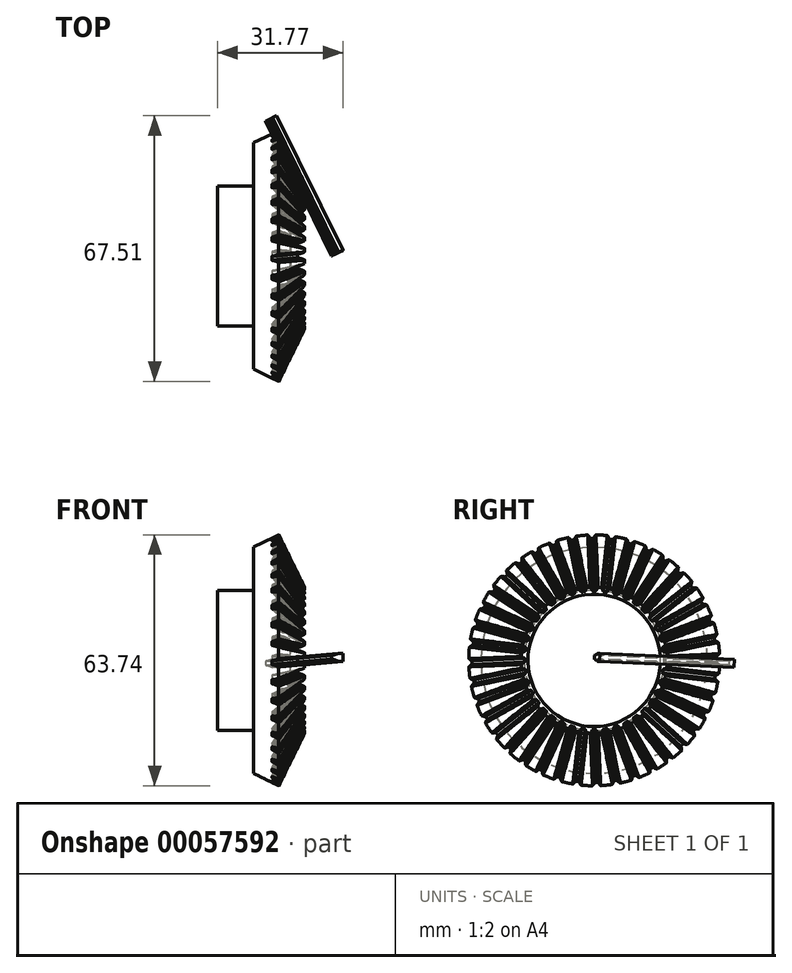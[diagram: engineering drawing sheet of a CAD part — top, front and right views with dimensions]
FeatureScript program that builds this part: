
annotation { "Feature Type Name" : "Feature", "Feature Type Description" : "" }
export const myFeature = defineFeature(function(context is Context, id is Id, definition is map)
    precondition{}
    {
        {
            var Q0;
            Q0=qCreatedBy(makeId("Top.planeOp"),FACE);
            var sketch = newSketch(context, id + "F0", { "sketchPlane" : qUnion([Q0])});
            skLineSegment(sketch, "E0.bottom", {"start": v(-8.92, 18.14) * mm, "end": v(9.22, 18.14) * mm, "construction": true});
            skLineSegment(sketch, "E0.right", {"start": v(9.22, 18.14) * mm, "end": v(8.92, -18.14) * mm, "construction": true});
            skLineSegment(sketch, "E1", {"start": v(-8.1, 18.54) * mm, "end": v(-11.62, 16.81) * mm});
            skLineSegment(sketch, "E2", {"start": v(-21.02, 28.75) * mm, "end": v(-14.67, 31.88) * mm});
            skLineSegment(sketch, "E3", {"start": v(-14.67, 31.88) * mm, "end": v(-8.1, 18.54) * mm});
            skLineSegment(sketch, "E4", {"start": v(-30.16, 0) * mm, "end": v(-30.16, 17.78) * mm});
            skLineSegment(sketch, "E5", {"start": v(-30.16, 17.78) * mm, "end": v(-21.02, 17.78) * mm});
            skLineSegment(sketch, "E6", {"start": v(-21.02, 17.78) * mm, "end": v(-21.02, 28.75) * mm});
            skPoint(sketch, "E7.orphan", {"position": v(-15.48, 31.48) * mm});
            skLineSegment(sketch, "E8", {"start": v(-11.62, 16.81) * mm, "end": v(-11.62, 0) * mm});
            skLineSegment(sketch, "E9", {"start": v(-11.62, 0) * mm, "end": v(-30.16, 0) * mm});
            skLineSegment(sketch, "E10", {"start": v(-9.86, 17.68) * mm, "end": v(-1.17, 0) * mm, "construction": true});
            skLineSegment(sketch, "E11", {"start": v(-1.17, 0) * mm, "end": v(0, 0) * mm});
            skLineSegment(sketch, "E12.trimOffspring", {"start": v(-8.92, 18.14) * mm, "end": v(0, 0) * mm, "construction": true});
            skPoint(sketch, "E13.orphan", {"position": v(-8.92, 18.14) * mm});
            skSolve(sketch);
        }
        {
            var Q0;
            Q0=makeQuery(id+"F0.imprint","IMPRINT",FACE,{"disambiguationData":[TD([[makeQuery(id+"F0.imprint","IMPRINT",EDGE,{"derivedFrom":sQuery(id+"F0.wireOp",EDGE,"E2")}),-1.0]])]});
            var Q1;
            Q1=sQuery(id+"F0.wireOp",EDGE,"E9");
            revolve(context, id + "F1", {"entities" : qUnion([Q0]), "axis" : qUnion([Q1]), "revolveType" : RevolveType.FULL});
        }
        {
            var Q0;
            Q0=sQuery(id+"F0.wireOp",EDGE,"E10");
            cPlane(context, id + "F2", {"entities" : qUnion([Q0]), "cplaneType" : CPlaneType.LINE_ANGLE, "offset" : 152.4 * mm, "angle" : 90 * degree, "width" : 152.4 * mm, "height" : 152.4 * mm});
        }
        {
            var Q0;
            Q0=sQuery(id+"F0.wireOp",EDGE,"E2");
            var Q1;
            Q1=makeQuery(id+"F0.imprint","IMPRINT",FACE,{"disambiguationData":[TD([[makeQuery(id+"F0.imprint","IMPRINT",EDGE,{"derivedFrom":sQuery(id+"F0.wireOp",EDGE,"E2")}),-1.0]])]});
            cPlane(context, id + "F3", {"entities" : qUnion([Q0, Q1]), "cplaneType" : CPlaneType.LINE_ANGLE, "offset" : 152.4 * mm, "angle" : 90 * degree, "width" : 152.4 * mm, "height" : 152.4 * mm});
        }
        {
            var Q0;
            Q0=qCreatedBy(makeId("Top.planeOp"),FACE);
            cPlane(context, id + "F4", {"entities" : qUnion([Q0]), "cplaneType" : CPlaneType.OFFSET, "offset" : 0.71 * mm, "width" : 152.4 * mm, "height" : 152.4 * mm});
        }
        {
            var Q0;
            Q0=sQuery(id+"F0.wireOp",VERTEX,"E10.end");
            var Q1;
            Q1=qCreatedBy(id+"F3.planeOp",FACE);
            cPlane(context, id + "F5", {"entities" : qUnion([Q0, Q1]), "cplaneType" : CPlaneType.PLANE_POINT, "offset" : 152.4 * mm, "width" : 152.4 * mm, "height" : 152.4 * mm});
        }
        {
            var Q0;
            Q0=qCreatedBy(id+"F4.planeOp",FACE);
            var sketch = newSketch(context, id + "F6", { "sketchPlane" : qUnion([Q0])});
            skLineSegment(sketch, "E14", {"start": v(-47.56, -22.82) * mm, "end": v(6.95, 4) * mm, "construction": true});
            skSolve(sketch);
        }
        {
            var Q0;
            Q0=sQuery(id+"F6.wireOp",EDGE,"E14");
            var Q1;
            Q1=qCreatedBy(id+"F5.planeOp",FACE);
            cPlane(context, id + "F7", {"entities" : qUnion([Q0, Q1]), "cplaneType" : CPlaneType.LINE_ANGLE, "offset" : 152.4 * mm, "angle" : 2.25 * degree, "width" : 152.4 * mm, "height" : 152.4 * mm});
        }
        {
            var Q0;
            Q0=qCreatedBy(id+"F5.planeOp",FACE);
            var sketch = newSketch(context, id + "F8", { "sketchPlane" : qUnion([Q0])});
            skLineSegment(sketch, "E15.MirrorCS", {"start": v(1.04, 0.45) * mm, "end": v(1.05, 0.42) * mm});
            skLineSegment(sketch, "E16.MirrorCS", {"start": v(0.96, 0.5) * mm, "end": v(1, 0.48) * mm});
            skLineSegment(sketch, "E17.MirrorCS", {"start": v(0.89, 0.53) * mm, "end": v(0.96, 0.5) * mm});
            skLineSegment(sketch, "E18.MirrorCS", {"start": v(1, 0.48) * mm, "end": v(1.04, 0.45) * mm});
            skLineSegment(sketch, "E19.MirrorCS", {"start": v(0.8, -0.56) * mm, "end": v(0.67, -0.57) * mm});
            skLineSegment(sketch, "E20.MirrorCS", {"start": v(0.89, -0.53) * mm, "end": v(0.8, -0.56) * mm});
            skLineSegment(sketch, "E21.MirrorCS", {"start": v(0.96, -0.5) * mm, "end": v(0.89, -0.53) * mm});
            skLineSegment(sketch, "E22.MirrorCS", {"start": v(-0.42, -0.85) * mm, "end": v(-0.54, -0.9) * mm});
            skLineSegment(sketch, "E23.MirrorCS", {"start": v(0.67, -0.57) * mm, "end": v(0.55, -0.59) * mm});
            skLineSegment(sketch, "E24.MirrorCS", {"start": v(0.3, -0.64) * mm, "end": v(0.18, -0.67) * mm});
            skLineSegment(sketch, "E25.MirrorCS", {"start": v(-0.54, -0.9) * mm, "end": v(-0.66, -0.94) * mm});
            skLineSegment(sketch, "E26.MirrorCS", {"start": v(1.05, -0.42) * mm, "end": v(1.04, -0.45) * mm});
            skLineSegment(sketch, "E27.MirrorCS", {"start": v(-0.3, -0.81) * mm, "end": v(-0.42, -0.85) * mm});
            skLineSegment(sketch, "E28.MirrorCS", {"start": v(0.42, -0.6) * mm, "end": v(0.3, -0.64) * mm});
            skLineSegment(sketch, "E29.MirrorCS", {"start": v(0.18, -0.67) * mm, "end": v(0.06, -0.7) * mm});
            skLineSegment(sketch, "E30.MirrorCS", {"start": v(-0.66, -0.94) * mm, "end": v(-0.78, -0.99) * mm});
            skLineSegment(sketch, "E31.MirrorCS", {"start": v(1.04, -0.45) * mm, "end": v(1, -0.48) * mm});
            skLineSegment(sketch, "E32.MirrorCS", {"start": v(0.55, -0.59) * mm, "end": v(0.42, -0.6) * mm});
            skLineSegment(sketch, "E33.MirrorCS", {"start": v(0.55, 0.59) * mm, "end": v(0.67, 0.57) * mm});
            skLineSegment(sketch, "E34.MirrorCS", {"start": v(0.42, 0.6) * mm, "end": v(0.55, 0.59) * mm});
            skLineSegment(sketch, "E35.MirrorCS", {"start": v(0.3, 0.64) * mm, "end": v(0.42, 0.6) * mm});
            skLineSegment(sketch, "E36.MirrorCS", {"start": v(0.18, 0.67) * mm, "end": v(0.3, 0.64) * mm});
            skLineSegment(sketch, "E37.MirrorCS", {"start": v(0.06, 0.7) * mm, "end": v(0.18, 0.67) * mm});
            skLineSegment(sketch, "E38.MirrorCS", {"start": v(-0.06, 0.73) * mm, "end": v(0.06, 0.7) * mm});
            skLineSegment(sketch, "E39.MirrorCS", {"start": v(-0.18, 0.77) * mm, "end": v(-0.06, 0.73) * mm});
            skLineSegment(sketch, "E40.MirrorCS", {"start": v(-0.3, 0.81) * mm, "end": v(-0.18, 0.77) * mm});
            skLineSegment(sketch, "E41.MirrorCS", {"start": v(-0.42, 0.85) * mm, "end": v(-0.3, 0.81) * mm});
            skLineSegment(sketch, "E42.MirrorCS", {"start": v(-0.54, 0.9) * mm, "end": v(-0.42, 0.85) * mm});
            skLineSegment(sketch, "E43.MirrorCS", {"start": v(-0.66, 0.94) * mm, "end": v(-0.54, 0.9) * mm});
            skLineSegment(sketch, "E44.MirrorCS", {"start": v(-0.06, -0.73) * mm, "end": v(-0.18, -0.77) * mm});
            skLineSegment(sketch, "E45.MirrorCS", {"start": v(-0.78, 0.99) * mm, "end": v(-0.66, 0.94) * mm});
            skLineSegment(sketch, "E46.MirrorCS", {"start": v(-0.9, 1.04) * mm, "end": v(-0.78, 0.99) * mm});
            skLineSegment(sketch, "E47.MirrorCS", {"start": v(0.8, 0.56) * mm, "end": v(0.89, 0.53) * mm});
            skLineSegment(sketch, "E48.MirrorCS", {"start": v(0.67, 0.57) * mm, "end": v(0.8, 0.56) * mm});
            skLineSegment(sketch, "E49.MirrorCS", {"start": v(-0.18, -0.77) * mm, "end": v(-0.3, -0.81) * mm});
            skLineSegment(sketch, "E50.MirrorCS", {"start": v(1, -0.48) * mm, "end": v(0.96, -0.5) * mm});
            skLineSegment(sketch, "E51.MirrorCS", {"start": v(0.06, -0.7) * mm, "end": v(-0.06, -0.73) * mm});
            skLineSegment(sketch, "E52.MirrorCS", {"start": v(-0.78, -0.99) * mm, "end": v(-0.9, -1.04) * mm});
            skLineSegment(sketch, "E53.MirrorCS", {"start": v(1.05, 0.42) * mm, "end": v(1.05, -0.42) * mm});
            skLineSegment(sketch, "E54.MirrorCS", {"start": v(-2.07, -1.04) * mm, "end": v(-0.9, -1.04) * mm});
            skLineSegment(sketch, "E55.MirrorCS", {"start": v(-0.9, 1.04) * mm, "end": v(-2.07, 1.04) * mm});
            skLineSegment(sketch, "E56.MirrorCS", {"start": v(-2.07, 1.04) * mm, "end": v(-2.07, -1.04) * mm});
            skSolve(sketch);
        }
        {
            var Q0;
            Q0=makeQuery(id+"F8.imprint","IMPRINT",FACE,{"disambiguationData":[TD([[makeQuery(id+"F8.imprint","IMPRINT",EDGE,{"derivedFrom":sQuery(id+"F8.wireOp",EDGE,"E15.MirrorCS")}),-1.0]])]});
            extrude(context, id + "F9", {"entities" : qUnion([Q0]), "operationType" : NewBodyOperationType.REMOVE, "depth" : 38.1 * mm});
        }
        {
            var Q0;
            Q0=qCreatedBy(id+"F7.planeOp",FACE);
            var sketch = newSketch(context, id + "F10", { "sketchPlane" : qUnion([Q0])});
            skLineSegment(sketch, "E57", {"start": v(0.88, 0.25) * mm, "end": v(0.76, 0.2) * mm});
            skLineSegment(sketch, "E58", {"start": v(0.76, 0.2) * mm, "end": v(0.64, 0.16) * mm});
            skLineSegment(sketch, "E59", {"start": v(0.64, 0.16) * mm, "end": v(0.53, 0.11) * mm});
            skLineSegment(sketch, "E60", {"start": v(0.53, 0.11) * mm, "end": v(0.4, 0.07) * mm});
            skLineSegment(sketch, "E61", {"start": v(0.4, 0.07) * mm, "end": v(0.29, 0.03) * mm});
            skLineSegment(sketch, "E62", {"start": v(0.29, 0.03) * mm, "end": v(0.17, -0.01) * mm});
            skLineSegment(sketch, "E63", {"start": v(0.17, -0.01) * mm, "end": v(0.05, -0.05) * mm});
            skLineSegment(sketch, "E64", {"start": v(0.05, -0.05) * mm, "end": v(-0.07, -0.09) * mm});
            skLineSegment(sketch, "E65", {"start": v(-0.07, -0.09) * mm, "end": v(-0.2, -0.12) * mm});
            skLineSegment(sketch, "E66", {"start": v(-0.2, -0.12) * mm, "end": v(-0.32, -0.15) * mm});
            skLineSegment(sketch, "E67", {"start": v(-0.32, -0.15) * mm, "end": v(-0.44, -0.18) * mm});
            skLineSegment(sketch, "E68", {"start": v(-0.44, -0.18) * mm, "end": v(-0.56, -0.2) * mm});
            skLineSegment(sketch, "E69", {"start": v(-0.56, -0.2) * mm, "end": v(-0.69, -0.22) * mm});
            skLineSegment(sketch, "E70", {"start": v(-0.69, -0.22) * mm, "end": v(-0.81, -0.23) * mm});
            skLineSegment(sketch, "E71", {"start": v(-0.81, -0.23) * mm, "end": v(-0.9, -0.25) * mm});
            skLineSegment(sketch, "E72", {"start": v(-0.9, -0.25) * mm, "end": v(-0.97, -0.28) * mm});
            skLineSegment(sketch, "E73", {"start": v(-0.97, -0.28) * mm, "end": v(-1.02, -0.3) * mm});
            skLineSegment(sketch, "E74", {"start": v(-1.02, -0.3) * mm, "end": v(-1.05, -0.33) * mm});
            skLineSegment(sketch, "E75", {"start": v(-1.05, -0.33) * mm, "end": v(-1.06, -0.36) * mm});
            skLineSegment(sketch, "E76", {"start": v(-1.06, -0.36) * mm, "end": v(-1.06, -1.2) * mm});
            skLineSegment(sketch, "E77", {"start": v(-1.06, -1.2) * mm, "end": v(-1.05, -1.24) * mm});
            skLineSegment(sketch, "E78", {"start": v(-1.05, -1.24) * mm, "end": v(-1.02, -1.27) * mm});
            skLineSegment(sketch, "E79", {"start": v(-1.02, -1.27) * mm, "end": v(-0.97, -1.3) * mm});
            skLineSegment(sketch, "E80", {"start": v(-0.97, -1.3) * mm, "end": v(-0.9, -1.32) * mm});
            skLineSegment(sketch, "E81", {"start": v(-0.9, -1.32) * mm, "end": v(-0.81, -1.34) * mm});
            skLineSegment(sketch, "E82", {"start": v(-0.81, -1.34) * mm, "end": v(-0.69, -1.35) * mm});
            skLineSegment(sketch, "E83", {"start": v(-0.69, -1.35) * mm, "end": v(-0.56, -1.37) * mm});
            skLineSegment(sketch, "E84", {"start": v(-0.56, -1.37) * mm, "end": v(-0.44, -1.4) * mm});
            skLineSegment(sketch, "E85", {"start": v(-0.44, -1.4) * mm, "end": v(-0.32, -1.42) * mm});
            skLineSegment(sketch, "E86", {"start": v(-0.32, -1.42) * mm, "end": v(-0.2, -1.45) * mm});
            skLineSegment(sketch, "E87", {"start": v(-0.2, -1.45) * mm, "end": v(-0.07, -1.48) * mm});
            skLineSegment(sketch, "E88", {"start": v(-0.07, -1.48) * mm, "end": v(0.05, -1.52) * mm});
            skLineSegment(sketch, "E89", {"start": v(0.05, -1.52) * mm, "end": v(0.17, -1.56) * mm});
            skLineSegment(sketch, "E90", {"start": v(0.17, -1.56) * mm, "end": v(0.29, -1.6) * mm});
            skLineSegment(sketch, "E91", {"start": v(0.29, -1.6) * mm, "end": v(0.4, -1.64) * mm});
            skLineSegment(sketch, "E92", {"start": v(0.4, -1.64) * mm, "end": v(0.53, -1.68) * mm});
            skLineSegment(sketch, "E93", {"start": v(0.53, -1.68) * mm, "end": v(0.64, -1.73) * mm});
            skLineSegment(sketch, "E94", {"start": v(0.64, -1.73) * mm, "end": v(0.76, -1.77) * mm});
            skLineSegment(sketch, "E95", {"start": v(0.76, -1.77) * mm, "end": v(0.88, -1.82) * mm});
            skLineSegment(sketch, "E96", {"start": v(0.88, 0.25) * mm, "end": v(2.06, 0.25) * mm});
            skLineSegment(sketch, "E97", {"start": v(2.06, 0.25) * mm, "end": v(2.06, -1.82) * mm});
            skLineSegment(sketch, "E98", {"start": v(2.06, -1.82) * mm, "end": v(0.88, -1.82) * mm});
            skSolve(sketch);
        }
        {
            var Q0;
            Q0=makeQuery(id+"F10.imprint","IMPRINT",FACE,{"disambiguationData":[TD([[makeQuery(id+"F10.imprint","IMPRINT",EDGE,{"derivedFrom":sQuery(id+"F10.wireOp",EDGE,"E57")}),1.0]])]});
            extrude(context, id + "F11", {"entities" : qUnion([Q0]), "oppositeDirection" : true, "depth" : 38.1 * mm});
        }
        {
            var Q0;
            Q0=qCreatedBy(makeId("Top.planeOp"),FACE);
            cPlane(context, id + "F12", {"entities" : qUnion([Q0]), "cplaneType" : CPlaneType.OFFSET, "offset" : 0.71 * mm, "oppositeDirection" : true, "width" : 152.4 * mm, "height" : 152.4 * mm});
        }
        {
            var Q0;
            Q0=qCreatedBy(id+"F12.planeOp",FACE);
            var sketch = newSketch(context, id + "F13", { "sketchPlane" : qUnion([Q0])});
            skLineSegment(sketch, "E99", {"start": v(-32.93, -15.62) * mm, "end": v(17.18, 9.02) * mm, "construction": true});
            skSolve(sketch);
        }
        {
            var Q0;
            Q0=sQuery(id+"F13.wireOp",EDGE,"E99");
            var Q1;
            Q1=qCreatedBy(id+"F5.planeOp",FACE);
            cPlane(context, id + "F14", {"entities" : qUnion([Q0, Q1]), "cplaneType" : CPlaneType.LINE_ANGLE, "offset" : 152.4 * mm, "angle" : 357.75 * degree, "width" : 152.4 * mm, "height" : 152.4 * mm});
        }
        {
            var Q0;
            Q0=qCreatedBy(id+"F14.planeOp",FACE);
            var sketch = newSketch(context, id + "F15", { "sketchPlane" : qUnion([Q0])});
            skLineSegment(sketch, "E100", {"start": v(0.88, 1.84) * mm, "end": v(0.77, 1.79) * mm});
            skLineSegment(sketch, "E101", {"start": v(0.77, 1.79) * mm, "end": v(0.65, 1.74) * mm});
            skLineSegment(sketch, "E102", {"start": v(0.65, 1.74) * mm, "end": v(0.53, 1.7) * mm});
            skLineSegment(sketch, "E103", {"start": v(0.53, 1.7) * mm, "end": v(0.42, 1.65) * mm});
            skLineSegment(sketch, "E104", {"start": v(0.42, 1.65) * mm, "end": v(0.3, 1.6) * mm});
            skLineSegment(sketch, "E105", {"start": v(0.3, 1.6) * mm, "end": v(0.18, 1.57) * mm});
            skLineSegment(sketch, "E106", {"start": v(0.18, 1.57) * mm, "end": v(0.06, 1.53) * mm});
            skLineSegment(sketch, "E107", {"start": v(0.06, 1.53) * mm, "end": v(-0.06, 1.5) * mm});
            skLineSegment(sketch, "E108", {"start": v(-0.06, 1.5) * mm, "end": v(-0.18, 1.46) * mm});
            skLineSegment(sketch, "E109", {"start": v(-0.18, 1.46) * mm, "end": v(-0.3, 1.43) * mm});
            skLineSegment(sketch, "E110", {"start": v(-0.3, 1.43) * mm, "end": v(-0.43, 1.4) * mm});
            skLineSegment(sketch, "E111", {"start": v(-0.43, 1.4) * mm, "end": v(-0.55, 1.38) * mm});
            skLineSegment(sketch, "E112", {"start": v(-0.55, 1.38) * mm, "end": v(-0.68, 1.37) * mm});
            skLineSegment(sketch, "E113", {"start": v(-0.68, 1.37) * mm, "end": v(-0.8, 1.35) * mm});
            skLineSegment(sketch, "E114", {"start": v(-0.8, 1.35) * mm, "end": v(-0.9, 1.33) * mm});
            skLineSegment(sketch, "E115", {"start": v(-0.9, 1.33) * mm, "end": v(-0.96, 1.3) * mm});
            skLineSegment(sketch, "E116", {"start": v(-0.96, 1.3) * mm, "end": v(-1.01, 1.28) * mm});
            skLineSegment(sketch, "E117", {"start": v(-1.01, 1.28) * mm, "end": v(-1.05, 1.25) * mm});
            skLineSegment(sketch, "E118", {"start": v(-1.05, 1.25) * mm, "end": v(-1.06, 1.22) * mm});
            skLineSegment(sketch, "E119", {"start": v(-1.06, 1.22) * mm, "end": v(-1.06, 0.37) * mm});
            skLineSegment(sketch, "E120", {"start": v(-1.06, 0.37) * mm, "end": v(-1.05, 0.35) * mm});
            skLineSegment(sketch, "E121", {"start": v(-1.05, 0.35) * mm, "end": v(-1.01, 0.32) * mm});
            skLineSegment(sketch, "E122", {"start": v(-1.01, 0.32) * mm, "end": v(-0.96, 0.3) * mm});
            skLineSegment(sketch, "E123", {"start": v(-0.96, 0.3) * mm, "end": v(-0.9, 0.27) * mm});
            skLineSegment(sketch, "E124", {"start": v(-0.9, 0.27) * mm, "end": v(-0.8, 0.24) * mm});
            skLineSegment(sketch, "E125", {"start": v(-0.8, 0.24) * mm, "end": v(-0.68, 0.23) * mm});
            skLineSegment(sketch, "E126", {"start": v(-0.68, 0.23) * mm, "end": v(-0.55, 0.21) * mm});
            skLineSegment(sketch, "E127", {"start": v(-0.55, 0.21) * mm, "end": v(-0.43, 0.19) * mm});
            skLineSegment(sketch, "E128", {"start": v(-0.43, 0.19) * mm, "end": v(-0.3, 0.16) * mm});
            skLineSegment(sketch, "E129", {"start": v(-0.3, 0.16) * mm, "end": v(-0.18, 0.13) * mm});
            skLineSegment(sketch, "E130", {"start": v(-0.18, 0.13) * mm, "end": v(-0.06, 0.1) * mm});
            skLineSegment(sketch, "E131", {"start": v(-0.06, 0.1) * mm, "end": v(0.06, 0.07) * mm});
            skLineSegment(sketch, "E132", {"start": v(0.06, 0.07) * mm, "end": v(0.18, 0.03) * mm});
            skLineSegment(sketch, "E133", {"start": v(0.18, 0.03) * mm, "end": v(0.3, -0.01) * mm});
            skLineSegment(sketch, "E134", {"start": v(0.3, -0.01) * mm, "end": v(0.42, -0.05) * mm});
            skLineSegment(sketch, "E135", {"start": v(0.42, -0.05) * mm, "end": v(0.53, -0.1) * mm});
            skLineSegment(sketch, "E136", {"start": v(0.53, -0.1) * mm, "end": v(0.65, -0.14) * mm});
            skLineSegment(sketch, "E137", {"start": v(0.65, -0.14) * mm, "end": v(0.77, -0.19) * mm});
            skLineSegment(sketch, "E138", {"start": v(0.77, -0.19) * mm, "end": v(0.88, -0.24) * mm});
            skLineSegment(sketch, "E139", {"start": v(0.88, 1.84) * mm, "end": v(2.07, 1.84) * mm});
            skLineSegment(sketch, "E140", {"start": v(2.07, 1.84) * mm, "end": v(2.07, -0.24) * mm});
            skLineSegment(sketch, "E141", {"start": v(2.07, -0.24) * mm, "end": v(0.88, -0.24) * mm});
            skSolve(sketch);
        }
        {
            var Q0;
            Q0 = qSketchRegion(id + "F15", true);
            extrude(context, id + "F16", {"entities" : qUnion([Q0]), "oppositeDirection" : true, "depth" : 38.1 * mm});
        }
        {
            var Q0;
            Q0=qCreatedBy(makeId("Top.planeOp"),FACE);
            var sketch = newSketch(context, id + "F17", { "sketchPlane" : qUnion([Q0])});
            skLineSegment(sketch, "E142", {"start": v(75.46, 0) * mm, "end": v(0.5, 0) * mm, "construction": true});
            skSolve(sketch);
        }
        {
            var Q0;
            Q0=makeQuery(id+"F11.opExtrude","SWEPT_BODY",BODY,{"disambiguationData":[OSD([sQuery(id+"F10.wireOp",EDGE,"E57"),sQuery(id+"F10.wireOp",EDGE,"E58"),sQuery(id+"F10.wireOp",EDGE,"E59"),sQuery(id+"F10.wireOp",EDGE,"E60"),sQuery(id+"F10.wireOp",EDGE,"E61"),sQuery(id+"F10.wireOp",EDGE,"E62"),sQuery(id+"F10.wireOp",EDGE,"E63"),sQuery(id+"F10.wireOp",EDGE,"E64"),sQuery(id+"F10.wireOp",EDGE,"E65"),sQuery(id+"F10.wireOp",EDGE,"E66"),sQuery(id+"F10.wireOp",EDGE,"E67"),sQuery(id+"F10.wireOp",EDGE,"E68"),sQuery(id+"F10.wireOp",EDGE,"E69"),sQuery(id+"F10.wireOp",EDGE,"E70"),sQuery(id+"F10.wireOp",EDGE,"E71"),sQuery(id+"F10.wireOp",EDGE,"E72"),sQuery(id+"F10.wireOp",EDGE,"E73"),sQuery(id+"F10.wireOp",EDGE,"E74"),sQuery(id+"F10.wireOp",EDGE,"E75"),sQuery(id+"F10.wireOp",EDGE,"E76"),sQuery(id+"F10.wireOp",EDGE,"E77"),sQuery(id+"F10.wireOp",EDGE,"E78"),sQuery(id+"F10.wireOp",EDGE,"E79"),sQuery(id+"F10.wireOp",EDGE,"E80"),sQuery(id+"F10.wireOp",EDGE,"E81"),sQuery(id+"F10.wireOp",EDGE,"E82"),sQuery(id+"F10.wireOp",EDGE,"E83"),sQuery(id+"F10.wireOp",EDGE,"E84"),sQuery(id+"F10.wireOp",EDGE,"E85"),sQuery(id+"F10.wireOp",EDGE,"E86"),sQuery(id+"F10.wireOp",EDGE,"E87"),sQuery(id+"F10.wireOp",EDGE,"E88"),sQuery(id+"F10.wireOp",EDGE,"E89"),sQuery(id+"F10.wireOp",EDGE,"E90"),sQuery(id+"F10.wireOp",EDGE,"E91"),sQuery(id+"F10.wireOp",EDGE,"E92"),sQuery(id+"F10.wireOp",EDGE,"E93"),sQuery(id+"F10.wireOp",EDGE,"E94"),sQuery(id+"F10.wireOp",EDGE,"E95"),sQuery(id+"F10.wireOp",EDGE,"E96"),sQuery(id+"F10.wireOp",EDGE,"E97"),sQuery(id+"F10.wireOp",EDGE,"E98")])]});
            var Q1;
            Q1=sQuery(id+"F17.wireOp",EDGE,"E142");
            circularPattern(context, id + "F18", {"entities" : qUnion([Q0]), "axis" : qUnion([Q1]), "angle" : 9 * degree, "instanceCount" : 40});
        }
        {
            var Q0;
            Q0=makeQuery(id+"F18.opPattern","COPY",BODY,{"derivedFrom":makeQuery(id+"F11.opExtrude","SWEPT_BODY",BODY,{"disambiguationData":[OSD([sQuery(id+"F10.wireOp",EDGE,"E57"),sQuery(id+"F10.wireOp",EDGE,"E58"),sQuery(id+"F10.wireOp",EDGE,"E59"),sQuery(id+"F10.wireOp",EDGE,"E60"),sQuery(id+"F10.wireOp",EDGE,"E61"),sQuery(id+"F10.wireOp",EDGE,"E62"),sQuery(id+"F10.wireOp",EDGE,"E63"),sQuery(id+"F10.wireOp",EDGE,"E64"),sQuery(id+"F10.wireOp",EDGE,"E65"),sQuery(id+"F10.wireOp",EDGE,"E66"),sQuery(id+"F10.wireOp",EDGE,"E67"),sQuery(id+"F10.wireOp",EDGE,"E68"),sQuery(id+"F10.wireOp",EDGE,"E69"),sQuery(id+"F10.wireOp",EDGE,"E70"),sQuery(id+"F10.wireOp",EDGE,"E71"),sQuery(id+"F10.wireOp",EDGE,"E72"),sQuery(id+"F10.wireOp",EDGE,"E73"),sQuery(id+"F10.wireOp",EDGE,"E74"),sQuery(id+"F10.wireOp",EDGE,"E75"),sQuery(id+"F10.wireOp",EDGE,"E76"),sQuery(id+"F10.wireOp",EDGE,"E77"),sQuery(id+"F10.wireOp",EDGE,"E78"),sQuery(id+"F10.wireOp",EDGE,"E79"),sQuery(id+"F10.wireOp",EDGE,"E80"),sQuery(id+"F10.wireOp",EDGE,"E81"),sQuery(id+"F10.wireOp",EDGE,"E82"),sQuery(id+"F10.wireOp",EDGE,"E83"),sQuery(id+"F10.wireOp",EDGE,"E84"),sQuery(id+"F10.wireOp",EDGE,"E85"),sQuery(id+"F10.wireOp",EDGE,"E86"),sQuery(id+"F10.wireOp",EDGE,"E87"),sQuery(id+"F10.wireOp",EDGE,"E88"),sQuery(id+"F10.wireOp",EDGE,"E89"),sQuery(id+"F10.wireOp",EDGE,"E90"),sQuery(id+"F10.wireOp",EDGE,"E91"),sQuery(id+"F10.wireOp",EDGE,"E92"),sQuery(id+"F10.wireOp",EDGE,"E93"),sQuery(id+"F10.wireOp",EDGE,"E94"),sQuery(id+"F10.wireOp",EDGE,"E95"),sQuery(id+"F10.wireOp",EDGE,"E96"),sQuery(id+"F10.wireOp",EDGE,"E97"),sQuery(id+"F10.wireOp",EDGE,"E98")])]}),"instanceName":"32"});
            var Q1;
            Q1=makeQuery(id+"F18.opPattern","COPY",BODY,{"derivedFrom":makeQuery(id+"F11.opExtrude","SWEPT_BODY",BODY,{"disambiguationData":[OSD([sQuery(id+"F10.wireOp",EDGE,"E57"),sQuery(id+"F10.wireOp",EDGE,"E58"),sQuery(id+"F10.wireOp",EDGE,"E59"),sQuery(id+"F10.wireOp",EDGE,"E60"),sQuery(id+"F10.wireOp",EDGE,"E61"),sQuery(id+"F10.wireOp",EDGE,"E62"),sQuery(id+"F10.wireOp",EDGE,"E63"),sQuery(id+"F10.wireOp",EDGE,"E64"),sQuery(id+"F10.wireOp",EDGE,"E65"),sQuery(id+"F10.wireOp",EDGE,"E66"),sQuery(id+"F10.wireOp",EDGE,"E67"),sQuery(id+"F10.wireOp",EDGE,"E68"),sQuery(id+"F10.wireOp",EDGE,"E69"),sQuery(id+"F10.wireOp",EDGE,"E70"),sQuery(id+"F10.wireOp",EDGE,"E71"),sQuery(id+"F10.wireOp",EDGE,"E72"),sQuery(id+"F10.wireOp",EDGE,"E73"),sQuery(id+"F10.wireOp",EDGE,"E74"),sQuery(id+"F10.wireOp",EDGE,"E75"),sQuery(id+"F10.wireOp",EDGE,"E76"),sQuery(id+"F10.wireOp",EDGE,"E77"),sQuery(id+"F10.wireOp",EDGE,"E78"),sQuery(id+"F10.wireOp",EDGE,"E79"),sQuery(id+"F10.wireOp",EDGE,"E80"),sQuery(id+"F10.wireOp",EDGE,"E81"),sQuery(id+"F10.wireOp",EDGE,"E82"),sQuery(id+"F10.wireOp",EDGE,"E83"),sQuery(id+"F10.wireOp",EDGE,"E84"),sQuery(id+"F10.wireOp",EDGE,"E85"),sQuery(id+"F10.wireOp",EDGE,"E86"),sQuery(id+"F10.wireOp",EDGE,"E87"),sQuery(id+"F10.wireOp",EDGE,"E88"),sQuery(id+"F10.wireOp",EDGE,"E89"),sQuery(id+"F10.wireOp",EDGE,"E90"),sQuery(id+"F10.wireOp",EDGE,"E91"),sQuery(id+"F10.wireOp",EDGE,"E92"),sQuery(id+"F10.wireOp",EDGE,"E93"),sQuery(id+"F10.wireOp",EDGE,"E94"),sQuery(id+"F10.wireOp",EDGE,"E95"),sQuery(id+"F10.wireOp",EDGE,"E96"),sQuery(id+"F10.wireOp",EDGE,"E97"),sQuery(id+"F10.wireOp",EDGE,"E98")])]}),"instanceName":"31"});
            var Q2;
            Q2=makeQuery(id+"F18.opPattern","COPY",BODY,{"derivedFrom":makeQuery(id+"F11.opExtrude","SWEPT_BODY",BODY,{"disambiguationData":[OSD([sQuery(id+"F10.wireOp",EDGE,"E57"),sQuery(id+"F10.wireOp",EDGE,"E58"),sQuery(id+"F10.wireOp",EDGE,"E59"),sQuery(id+"F10.wireOp",EDGE,"E60"),sQuery(id+"F10.wireOp",EDGE,"E61"),sQuery(id+"F10.wireOp",EDGE,"E62"),sQuery(id+"F10.wireOp",EDGE,"E63"),sQuery(id+"F10.wireOp",EDGE,"E64"),sQuery(id+"F10.wireOp",EDGE,"E65"),sQuery(id+"F10.wireOp",EDGE,"E66"),sQuery(id+"F10.wireOp",EDGE,"E67"),sQuery(id+"F10.wireOp",EDGE,"E68"),sQuery(id+"F10.wireOp",EDGE,"E69"),sQuery(id+"F10.wireOp",EDGE,"E70"),sQuery(id+"F10.wireOp",EDGE,"E71"),sQuery(id+"F10.wireOp",EDGE,"E72"),sQuery(id+"F10.wireOp",EDGE,"E73"),sQuery(id+"F10.wireOp",EDGE,"E74"),sQuery(id+"F10.wireOp",EDGE,"E75"),sQuery(id+"F10.wireOp",EDGE,"E76"),sQuery(id+"F10.wireOp",EDGE,"E77"),sQuery(id+"F10.wireOp",EDGE,"E78"),sQuery(id+"F10.wireOp",EDGE,"E79"),sQuery(id+"F10.wireOp",EDGE,"E80"),sQuery(id+"F10.wireOp",EDGE,"E81"),sQuery(id+"F10.wireOp",EDGE,"E82"),sQuery(id+"F10.wireOp",EDGE,"E83"),sQuery(id+"F10.wireOp",EDGE,"E84"),sQuery(id+"F10.wireOp",EDGE,"E85"),sQuery(id+"F10.wireOp",EDGE,"E86"),sQuery(id+"F10.wireOp",EDGE,"E87"),sQuery(id+"F10.wireOp",EDGE,"E88"),sQuery(id+"F10.wireOp",EDGE,"E89"),sQuery(id+"F10.wireOp",EDGE,"E90"),sQuery(id+"F10.wireOp",EDGE,"E91"),sQuery(id+"F10.wireOp",EDGE,"E92"),sQuery(id+"F10.wireOp",EDGE,"E93"),sQuery(id+"F10.wireOp",EDGE,"E94"),sQuery(id+"F10.wireOp",EDGE,"E95"),sQuery(id+"F10.wireOp",EDGE,"E96"),sQuery(id+"F10.wireOp",EDGE,"E97"),sQuery(id+"F10.wireOp",EDGE,"E98")])]}),"instanceName":"30"});
            var Q3;
            Q3=makeQuery(id+"F18.opPattern","COPY",BODY,{"derivedFrom":makeQuery(id+"F11.opExtrude","SWEPT_BODY",BODY,{"disambiguationData":[OSD([sQuery(id+"F10.wireOp",EDGE,"E57"),sQuery(id+"F10.wireOp",EDGE,"E58"),sQuery(id+"F10.wireOp",EDGE,"E59"),sQuery(id+"F10.wireOp",EDGE,"E60"),sQuery(id+"F10.wireOp",EDGE,"E61"),sQuery(id+"F10.wireOp",EDGE,"E62"),sQuery(id+"F10.wireOp",EDGE,"E63"),sQuery(id+"F10.wireOp",EDGE,"E64"),sQuery(id+"F10.wireOp",EDGE,"E65"),sQuery(id+"F10.wireOp",EDGE,"E66"),sQuery(id+"F10.wireOp",EDGE,"E67"),sQuery(id+"F10.wireOp",EDGE,"E68"),sQuery(id+"F10.wireOp",EDGE,"E69"),sQuery(id+"F10.wireOp",EDGE,"E70"),sQuery(id+"F10.wireOp",EDGE,"E71"),sQuery(id+"F10.wireOp",EDGE,"E72"),sQuery(id+"F10.wireOp",EDGE,"E73"),sQuery(id+"F10.wireOp",EDGE,"E74"),sQuery(id+"F10.wireOp",EDGE,"E75"),sQuery(id+"F10.wireOp",EDGE,"E76"),sQuery(id+"F10.wireOp",EDGE,"E77"),sQuery(id+"F10.wireOp",EDGE,"E78"),sQuery(id+"F10.wireOp",EDGE,"E79"),sQuery(id+"F10.wireOp",EDGE,"E80"),sQuery(id+"F10.wireOp",EDGE,"E81"),sQuery(id+"F10.wireOp",EDGE,"E82"),sQuery(id+"F10.wireOp",EDGE,"E83"),sQuery(id+"F10.wireOp",EDGE,"E84"),sQuery(id+"F10.wireOp",EDGE,"E85"),sQuery(id+"F10.wireOp",EDGE,"E86"),sQuery(id+"F10.wireOp",EDGE,"E87"),sQuery(id+"F10.wireOp",EDGE,"E88"),sQuery(id+"F10.wireOp",EDGE,"E89"),sQuery(id+"F10.wireOp",EDGE,"E90"),sQuery(id+"F10.wireOp",EDGE,"E91"),sQuery(id+"F10.wireOp",EDGE,"E92"),sQuery(id+"F10.wireOp",EDGE,"E93"),sQuery(id+"F10.wireOp",EDGE,"E94"),sQuery(id+"F10.wireOp",EDGE,"E95"),sQuery(id+"F10.wireOp",EDGE,"E96"),sQuery(id+"F10.wireOp",EDGE,"E97"),sQuery(id+"F10.wireOp",EDGE,"E98")])]}),"instanceName":"29"});
            var Q4;
            Q4=makeQuery(id+"F18.opPattern","COPY",BODY,{"derivedFrom":makeQuery(id+"F11.opExtrude","SWEPT_BODY",BODY,{"disambiguationData":[OSD([sQuery(id+"F10.wireOp",EDGE,"E57"),sQuery(id+"F10.wireOp",EDGE,"E58"),sQuery(id+"F10.wireOp",EDGE,"E59"),sQuery(id+"F10.wireOp",EDGE,"E60"),sQuery(id+"F10.wireOp",EDGE,"E61"),sQuery(id+"F10.wireOp",EDGE,"E62"),sQuery(id+"F10.wireOp",EDGE,"E63"),sQuery(id+"F10.wireOp",EDGE,"E64"),sQuery(id+"F10.wireOp",EDGE,"E65"),sQuery(id+"F10.wireOp",EDGE,"E66"),sQuery(id+"F10.wireOp",EDGE,"E67"),sQuery(id+"F10.wireOp",EDGE,"E68"),sQuery(id+"F10.wireOp",EDGE,"E69"),sQuery(id+"F10.wireOp",EDGE,"E70"),sQuery(id+"F10.wireOp",EDGE,"E71"),sQuery(id+"F10.wireOp",EDGE,"E72"),sQuery(id+"F10.wireOp",EDGE,"E73"),sQuery(id+"F10.wireOp",EDGE,"E74"),sQuery(id+"F10.wireOp",EDGE,"E75"),sQuery(id+"F10.wireOp",EDGE,"E76"),sQuery(id+"F10.wireOp",EDGE,"E77"),sQuery(id+"F10.wireOp",EDGE,"E78"),sQuery(id+"F10.wireOp",EDGE,"E79"),sQuery(id+"F10.wireOp",EDGE,"E80"),sQuery(id+"F10.wireOp",EDGE,"E81"),sQuery(id+"F10.wireOp",EDGE,"E82"),sQuery(id+"F10.wireOp",EDGE,"E83"),sQuery(id+"F10.wireOp",EDGE,"E84"),sQuery(id+"F10.wireOp",EDGE,"E85"),sQuery(id+"F10.wireOp",EDGE,"E86"),sQuery(id+"F10.wireOp",EDGE,"E87"),sQuery(id+"F10.wireOp",EDGE,"E88"),sQuery(id+"F10.wireOp",EDGE,"E89"),sQuery(id+"F10.wireOp",EDGE,"E90"),sQuery(id+"F10.wireOp",EDGE,"E91"),sQuery(id+"F10.wireOp",EDGE,"E92"),sQuery(id+"F10.wireOp",EDGE,"E93"),sQuery(id+"F10.wireOp",EDGE,"E94"),sQuery(id+"F10.wireOp",EDGE,"E95"),sQuery(id+"F10.wireOp",EDGE,"E96"),sQuery(id+"F10.wireOp",EDGE,"E97"),sQuery(id+"F10.wireOp",EDGE,"E98")])]}),"instanceName":"28"});
            var Q5;
            Q5=makeQuery(id+"F18.opPattern","COPY",BODY,{"derivedFrom":makeQuery(id+"F11.opExtrude","SWEPT_BODY",BODY,{"disambiguationData":[OSD([sQuery(id+"F10.wireOp",EDGE,"E57"),sQuery(id+"F10.wireOp",EDGE,"E58"),sQuery(id+"F10.wireOp",EDGE,"E59"),sQuery(id+"F10.wireOp",EDGE,"E60"),sQuery(id+"F10.wireOp",EDGE,"E61"),sQuery(id+"F10.wireOp",EDGE,"E62"),sQuery(id+"F10.wireOp",EDGE,"E63"),sQuery(id+"F10.wireOp",EDGE,"E64"),sQuery(id+"F10.wireOp",EDGE,"E65"),sQuery(id+"F10.wireOp",EDGE,"E66"),sQuery(id+"F10.wireOp",EDGE,"E67"),sQuery(id+"F10.wireOp",EDGE,"E68"),sQuery(id+"F10.wireOp",EDGE,"E69"),sQuery(id+"F10.wireOp",EDGE,"E70"),sQuery(id+"F10.wireOp",EDGE,"E71"),sQuery(id+"F10.wireOp",EDGE,"E72"),sQuery(id+"F10.wireOp",EDGE,"E73"),sQuery(id+"F10.wireOp",EDGE,"E74"),sQuery(id+"F10.wireOp",EDGE,"E75"),sQuery(id+"F10.wireOp",EDGE,"E76"),sQuery(id+"F10.wireOp",EDGE,"E77"),sQuery(id+"F10.wireOp",EDGE,"E78"),sQuery(id+"F10.wireOp",EDGE,"E79"),sQuery(id+"F10.wireOp",EDGE,"E80"),sQuery(id+"F10.wireOp",EDGE,"E81"),sQuery(id+"F10.wireOp",EDGE,"E82"),sQuery(id+"F10.wireOp",EDGE,"E83"),sQuery(id+"F10.wireOp",EDGE,"E84"),sQuery(id+"F10.wireOp",EDGE,"E85"),sQuery(id+"F10.wireOp",EDGE,"E86"),sQuery(id+"F10.wireOp",EDGE,"E87"),sQuery(id+"F10.wireOp",EDGE,"E88"),sQuery(id+"F10.wireOp",EDGE,"E89"),sQuery(id+"F10.wireOp",EDGE,"E90"),sQuery(id+"F10.wireOp",EDGE,"E91"),sQuery(id+"F10.wireOp",EDGE,"E92"),sQuery(id+"F10.wireOp",EDGE,"E93"),sQuery(id+"F10.wireOp",EDGE,"E94"),sQuery(id+"F10.wireOp",EDGE,"E95"),sQuery(id+"F10.wireOp",EDGE,"E96"),sQuery(id+"F10.wireOp",EDGE,"E97"),sQuery(id+"F10.wireOp",EDGE,"E98")])]}),"instanceName":"27"});
            var Q6;
            Q6=makeQuery(id+"F18.opPattern","COPY",BODY,{"derivedFrom":makeQuery(id+"F11.opExtrude","SWEPT_BODY",BODY,{"disambiguationData":[OSD([sQuery(id+"F10.wireOp",EDGE,"E57"),sQuery(id+"F10.wireOp",EDGE,"E58"),sQuery(id+"F10.wireOp",EDGE,"E59"),sQuery(id+"F10.wireOp",EDGE,"E60"),sQuery(id+"F10.wireOp",EDGE,"E61"),sQuery(id+"F10.wireOp",EDGE,"E62"),sQuery(id+"F10.wireOp",EDGE,"E63"),sQuery(id+"F10.wireOp",EDGE,"E64"),sQuery(id+"F10.wireOp",EDGE,"E65"),sQuery(id+"F10.wireOp",EDGE,"E66"),sQuery(id+"F10.wireOp",EDGE,"E67"),sQuery(id+"F10.wireOp",EDGE,"E68"),sQuery(id+"F10.wireOp",EDGE,"E69"),sQuery(id+"F10.wireOp",EDGE,"E70"),sQuery(id+"F10.wireOp",EDGE,"E71"),sQuery(id+"F10.wireOp",EDGE,"E72"),sQuery(id+"F10.wireOp",EDGE,"E73"),sQuery(id+"F10.wireOp",EDGE,"E74"),sQuery(id+"F10.wireOp",EDGE,"E75"),sQuery(id+"F10.wireOp",EDGE,"E76"),sQuery(id+"F10.wireOp",EDGE,"E77"),sQuery(id+"F10.wireOp",EDGE,"E78"),sQuery(id+"F10.wireOp",EDGE,"E79"),sQuery(id+"F10.wireOp",EDGE,"E80"),sQuery(id+"F10.wireOp",EDGE,"E81"),sQuery(id+"F10.wireOp",EDGE,"E82"),sQuery(id+"F10.wireOp",EDGE,"E83"),sQuery(id+"F10.wireOp",EDGE,"E84"),sQuery(id+"F10.wireOp",EDGE,"E85"),sQuery(id+"F10.wireOp",EDGE,"E86"),sQuery(id+"F10.wireOp",EDGE,"E87"),sQuery(id+"F10.wireOp",EDGE,"E88"),sQuery(id+"F10.wireOp",EDGE,"E89"),sQuery(id+"F10.wireOp",EDGE,"E90"),sQuery(id+"F10.wireOp",EDGE,"E91"),sQuery(id+"F10.wireOp",EDGE,"E92"),sQuery(id+"F10.wireOp",EDGE,"E93"),sQuery(id+"F10.wireOp",EDGE,"E94"),sQuery(id+"F10.wireOp",EDGE,"E95"),sQuery(id+"F10.wireOp",EDGE,"E96"),sQuery(id+"F10.wireOp",EDGE,"E97"),sQuery(id+"F10.wireOp",EDGE,"E98")])]}),"instanceName":"26"});
            var Q7;
            Q7=makeQuery(id+"F18.opPattern","COPY",BODY,{"derivedFrom":makeQuery(id+"F11.opExtrude","SWEPT_BODY",BODY,{"disambiguationData":[OSD([sQuery(id+"F10.wireOp",EDGE,"E57"),sQuery(id+"F10.wireOp",EDGE,"E58"),sQuery(id+"F10.wireOp",EDGE,"E59"),sQuery(id+"F10.wireOp",EDGE,"E60"),sQuery(id+"F10.wireOp",EDGE,"E61"),sQuery(id+"F10.wireOp",EDGE,"E62"),sQuery(id+"F10.wireOp",EDGE,"E63"),sQuery(id+"F10.wireOp",EDGE,"E64"),sQuery(id+"F10.wireOp",EDGE,"E65"),sQuery(id+"F10.wireOp",EDGE,"E66"),sQuery(id+"F10.wireOp",EDGE,"E67"),sQuery(id+"F10.wireOp",EDGE,"E68"),sQuery(id+"F10.wireOp",EDGE,"E69"),sQuery(id+"F10.wireOp",EDGE,"E70"),sQuery(id+"F10.wireOp",EDGE,"E71"),sQuery(id+"F10.wireOp",EDGE,"E72"),sQuery(id+"F10.wireOp",EDGE,"E73"),sQuery(id+"F10.wireOp",EDGE,"E74"),sQuery(id+"F10.wireOp",EDGE,"E75"),sQuery(id+"F10.wireOp",EDGE,"E76"),sQuery(id+"F10.wireOp",EDGE,"E77"),sQuery(id+"F10.wireOp",EDGE,"E78"),sQuery(id+"F10.wireOp",EDGE,"E79"),sQuery(id+"F10.wireOp",EDGE,"E80"),sQuery(id+"F10.wireOp",EDGE,"E81"),sQuery(id+"F10.wireOp",EDGE,"E82"),sQuery(id+"F10.wireOp",EDGE,"E83"),sQuery(id+"F10.wireOp",EDGE,"E84"),sQuery(id+"F10.wireOp",EDGE,"E85"),sQuery(id+"F10.wireOp",EDGE,"E86"),sQuery(id+"F10.wireOp",EDGE,"E87"),sQuery(id+"F10.wireOp",EDGE,"E88"),sQuery(id+"F10.wireOp",EDGE,"E89"),sQuery(id+"F10.wireOp",EDGE,"E90"),sQuery(id+"F10.wireOp",EDGE,"E91"),sQuery(id+"F10.wireOp",EDGE,"E92"),sQuery(id+"F10.wireOp",EDGE,"E93"),sQuery(id+"F10.wireOp",EDGE,"E94"),sQuery(id+"F10.wireOp",EDGE,"E95"),sQuery(id+"F10.wireOp",EDGE,"E96"),sQuery(id+"F10.wireOp",EDGE,"E97"),sQuery(id+"F10.wireOp",EDGE,"E98")])]}),"instanceName":"25"});
            var Q8;
            Q8=makeQuery(id+"F18.opPattern","COPY",BODY,{"derivedFrom":makeQuery(id+"F11.opExtrude","SWEPT_BODY",BODY,{"disambiguationData":[OSD([sQuery(id+"F10.wireOp",EDGE,"E57"),sQuery(id+"F10.wireOp",EDGE,"E58"),sQuery(id+"F10.wireOp",EDGE,"E59"),sQuery(id+"F10.wireOp",EDGE,"E60"),sQuery(id+"F10.wireOp",EDGE,"E61"),sQuery(id+"F10.wireOp",EDGE,"E62"),sQuery(id+"F10.wireOp",EDGE,"E63"),sQuery(id+"F10.wireOp",EDGE,"E64"),sQuery(id+"F10.wireOp",EDGE,"E65"),sQuery(id+"F10.wireOp",EDGE,"E66"),sQuery(id+"F10.wireOp",EDGE,"E67"),sQuery(id+"F10.wireOp",EDGE,"E68"),sQuery(id+"F10.wireOp",EDGE,"E69"),sQuery(id+"F10.wireOp",EDGE,"E70"),sQuery(id+"F10.wireOp",EDGE,"E71"),sQuery(id+"F10.wireOp",EDGE,"E72"),sQuery(id+"F10.wireOp",EDGE,"E73"),sQuery(id+"F10.wireOp",EDGE,"E74"),sQuery(id+"F10.wireOp",EDGE,"E75"),sQuery(id+"F10.wireOp",EDGE,"E76"),sQuery(id+"F10.wireOp",EDGE,"E77"),sQuery(id+"F10.wireOp",EDGE,"E78"),sQuery(id+"F10.wireOp",EDGE,"E79"),sQuery(id+"F10.wireOp",EDGE,"E80"),sQuery(id+"F10.wireOp",EDGE,"E81"),sQuery(id+"F10.wireOp",EDGE,"E82"),sQuery(id+"F10.wireOp",EDGE,"E83"),sQuery(id+"F10.wireOp",EDGE,"E84"),sQuery(id+"F10.wireOp",EDGE,"E85"),sQuery(id+"F10.wireOp",EDGE,"E86"),sQuery(id+"F10.wireOp",EDGE,"E87"),sQuery(id+"F10.wireOp",EDGE,"E88"),sQuery(id+"F10.wireOp",EDGE,"E89"),sQuery(id+"F10.wireOp",EDGE,"E90"),sQuery(id+"F10.wireOp",EDGE,"E91"),sQuery(id+"F10.wireOp",EDGE,"E92"),sQuery(id+"F10.wireOp",EDGE,"E93"),sQuery(id+"F10.wireOp",EDGE,"E94"),sQuery(id+"F10.wireOp",EDGE,"E95"),sQuery(id+"F10.wireOp",EDGE,"E96"),sQuery(id+"F10.wireOp",EDGE,"E97"),sQuery(id+"F10.wireOp",EDGE,"E98")])]}),"instanceName":"24"});
            var Q9;
            Q9=makeQuery(id+"F1.opRevolve","SWEPT_BODY",BODY,{"disambiguationData":[OSD([sQuery(id+"F0.wireOp",EDGE,"E1"),sQuery(id+"F0.wireOp",EDGE,"E2"),sQuery(id+"F0.wireOp",EDGE,"E3"),sQuery(id+"F0.wireOp",EDGE,"E4"),sQuery(id+"F0.wireOp",EDGE,"E5"),sQuery(id+"F0.wireOp",EDGE,"E6"),sQuery(id+"F0.wireOp",EDGE,"E8"),sQuery(id+"F0.wireOp",EDGE,"E9")])]});
            booleanBodies(context, id + "F19", {"operationType" : BooleanOperationType.SUBTRACTION, "tools" : qUnion([Q0, Q1, Q2, Q3, Q4, Q5, Q6, Q7, Q8]), "targets" : qUnion([Q9])});
        }
        {
            var Q0;
            Q0=makeQuery(id+"F18.opPattern","COPY",BODY,{"derivedFrom":makeQuery(id+"F11.opExtrude","SWEPT_BODY",BODY,{"disambiguationData":[OSD([sQuery(id+"F10.wireOp",EDGE,"E57"),sQuery(id+"F10.wireOp",EDGE,"E58"),sQuery(id+"F10.wireOp",EDGE,"E59"),sQuery(id+"F10.wireOp",EDGE,"E60"),sQuery(id+"F10.wireOp",EDGE,"E61"),sQuery(id+"F10.wireOp",EDGE,"E62"),sQuery(id+"F10.wireOp",EDGE,"E63"),sQuery(id+"F10.wireOp",EDGE,"E64"),sQuery(id+"F10.wireOp",EDGE,"E65"),sQuery(id+"F10.wireOp",EDGE,"E66"),sQuery(id+"F10.wireOp",EDGE,"E67"),sQuery(id+"F10.wireOp",EDGE,"E68"),sQuery(id+"F10.wireOp",EDGE,"E69"),sQuery(id+"F10.wireOp",EDGE,"E70"),sQuery(id+"F10.wireOp",EDGE,"E71"),sQuery(id+"F10.wireOp",EDGE,"E72"),sQuery(id+"F10.wireOp",EDGE,"E73"),sQuery(id+"F10.wireOp",EDGE,"E74"),sQuery(id+"F10.wireOp",EDGE,"E75"),sQuery(id+"F10.wireOp",EDGE,"E76"),sQuery(id+"F10.wireOp",EDGE,"E77"),sQuery(id+"F10.wireOp",EDGE,"E78"),sQuery(id+"F10.wireOp",EDGE,"E79"),sQuery(id+"F10.wireOp",EDGE,"E80"),sQuery(id+"F10.wireOp",EDGE,"E81"),sQuery(id+"F10.wireOp",EDGE,"E82"),sQuery(id+"F10.wireOp",EDGE,"E83"),sQuery(id+"F10.wireOp",EDGE,"E84"),sQuery(id+"F10.wireOp",EDGE,"E85"),sQuery(id+"F10.wireOp",EDGE,"E86"),sQuery(id+"F10.wireOp",EDGE,"E87"),sQuery(id+"F10.wireOp",EDGE,"E88"),sQuery(id+"F10.wireOp",EDGE,"E89"),sQuery(id+"F10.wireOp",EDGE,"E90"),sQuery(id+"F10.wireOp",EDGE,"E91"),sQuery(id+"F10.wireOp",EDGE,"E92"),sQuery(id+"F10.wireOp",EDGE,"E93"),sQuery(id+"F10.wireOp",EDGE,"E94"),sQuery(id+"F10.wireOp",EDGE,"E95"),sQuery(id+"F10.wireOp",EDGE,"E96"),sQuery(id+"F10.wireOp",EDGE,"E97"),sQuery(id+"F10.wireOp",EDGE,"E98")])]}),"instanceName":"23"});
            var Q1;
            Q1=makeQuery(id+"F18.opPattern","COPY",BODY,{"derivedFrom":makeQuery(id+"F11.opExtrude","SWEPT_BODY",BODY,{"disambiguationData":[OSD([sQuery(id+"F10.wireOp",EDGE,"E57"),sQuery(id+"F10.wireOp",EDGE,"E58"),sQuery(id+"F10.wireOp",EDGE,"E59"),sQuery(id+"F10.wireOp",EDGE,"E60"),sQuery(id+"F10.wireOp",EDGE,"E61"),sQuery(id+"F10.wireOp",EDGE,"E62"),sQuery(id+"F10.wireOp",EDGE,"E63"),sQuery(id+"F10.wireOp",EDGE,"E64"),sQuery(id+"F10.wireOp",EDGE,"E65"),sQuery(id+"F10.wireOp",EDGE,"E66"),sQuery(id+"F10.wireOp",EDGE,"E67"),sQuery(id+"F10.wireOp",EDGE,"E68"),sQuery(id+"F10.wireOp",EDGE,"E69"),sQuery(id+"F10.wireOp",EDGE,"E70"),sQuery(id+"F10.wireOp",EDGE,"E71"),sQuery(id+"F10.wireOp",EDGE,"E72"),sQuery(id+"F10.wireOp",EDGE,"E73"),sQuery(id+"F10.wireOp",EDGE,"E74"),sQuery(id+"F10.wireOp",EDGE,"E75"),sQuery(id+"F10.wireOp",EDGE,"E76"),sQuery(id+"F10.wireOp",EDGE,"E77"),sQuery(id+"F10.wireOp",EDGE,"E78"),sQuery(id+"F10.wireOp",EDGE,"E79"),sQuery(id+"F10.wireOp",EDGE,"E80"),sQuery(id+"F10.wireOp",EDGE,"E81"),sQuery(id+"F10.wireOp",EDGE,"E82"),sQuery(id+"F10.wireOp",EDGE,"E83"),sQuery(id+"F10.wireOp",EDGE,"E84"),sQuery(id+"F10.wireOp",EDGE,"E85"),sQuery(id+"F10.wireOp",EDGE,"E86"),sQuery(id+"F10.wireOp",EDGE,"E87"),sQuery(id+"F10.wireOp",EDGE,"E88"),sQuery(id+"F10.wireOp",EDGE,"E89"),sQuery(id+"F10.wireOp",EDGE,"E90"),sQuery(id+"F10.wireOp",EDGE,"E91"),sQuery(id+"F10.wireOp",EDGE,"E92"),sQuery(id+"F10.wireOp",EDGE,"E93"),sQuery(id+"F10.wireOp",EDGE,"E94"),sQuery(id+"F10.wireOp",EDGE,"E95"),sQuery(id+"F10.wireOp",EDGE,"E96"),sQuery(id+"F10.wireOp",EDGE,"E97"),sQuery(id+"F10.wireOp",EDGE,"E98")])]}),"instanceName":"22"});
            var Q2;
            Q2=makeQuery(id+"F18.opPattern","COPY",BODY,{"derivedFrom":makeQuery(id+"F11.opExtrude","SWEPT_BODY",BODY,{"disambiguationData":[OSD([sQuery(id+"F10.wireOp",EDGE,"E57"),sQuery(id+"F10.wireOp",EDGE,"E58"),sQuery(id+"F10.wireOp",EDGE,"E59"),sQuery(id+"F10.wireOp",EDGE,"E60"),sQuery(id+"F10.wireOp",EDGE,"E61"),sQuery(id+"F10.wireOp",EDGE,"E62"),sQuery(id+"F10.wireOp",EDGE,"E63"),sQuery(id+"F10.wireOp",EDGE,"E64"),sQuery(id+"F10.wireOp",EDGE,"E65"),sQuery(id+"F10.wireOp",EDGE,"E66"),sQuery(id+"F10.wireOp",EDGE,"E67"),sQuery(id+"F10.wireOp",EDGE,"E68"),sQuery(id+"F10.wireOp",EDGE,"E69"),sQuery(id+"F10.wireOp",EDGE,"E70"),sQuery(id+"F10.wireOp",EDGE,"E71"),sQuery(id+"F10.wireOp",EDGE,"E72"),sQuery(id+"F10.wireOp",EDGE,"E73"),sQuery(id+"F10.wireOp",EDGE,"E74"),sQuery(id+"F10.wireOp",EDGE,"E75"),sQuery(id+"F10.wireOp",EDGE,"E76"),sQuery(id+"F10.wireOp",EDGE,"E77"),sQuery(id+"F10.wireOp",EDGE,"E78"),sQuery(id+"F10.wireOp",EDGE,"E79"),sQuery(id+"F10.wireOp",EDGE,"E80"),sQuery(id+"F10.wireOp",EDGE,"E81"),sQuery(id+"F10.wireOp",EDGE,"E82"),sQuery(id+"F10.wireOp",EDGE,"E83"),sQuery(id+"F10.wireOp",EDGE,"E84"),sQuery(id+"F10.wireOp",EDGE,"E85"),sQuery(id+"F10.wireOp",EDGE,"E86"),sQuery(id+"F10.wireOp",EDGE,"E87"),sQuery(id+"F10.wireOp",EDGE,"E88"),sQuery(id+"F10.wireOp",EDGE,"E89"),sQuery(id+"F10.wireOp",EDGE,"E90"),sQuery(id+"F10.wireOp",EDGE,"E91"),sQuery(id+"F10.wireOp",EDGE,"E92"),sQuery(id+"F10.wireOp",EDGE,"E93"),sQuery(id+"F10.wireOp",EDGE,"E94"),sQuery(id+"F10.wireOp",EDGE,"E95"),sQuery(id+"F10.wireOp",EDGE,"E96"),sQuery(id+"F10.wireOp",EDGE,"E97"),sQuery(id+"F10.wireOp",EDGE,"E98")])]}),"instanceName":"21"});
            var Q3;
            Q3=makeQuery(id+"F18.opPattern","COPY",BODY,{"derivedFrom":makeQuery(id+"F11.opExtrude","SWEPT_BODY",BODY,{"disambiguationData":[OSD([sQuery(id+"F10.wireOp",EDGE,"E57"),sQuery(id+"F10.wireOp",EDGE,"E58"),sQuery(id+"F10.wireOp",EDGE,"E59"),sQuery(id+"F10.wireOp",EDGE,"E60"),sQuery(id+"F10.wireOp",EDGE,"E61"),sQuery(id+"F10.wireOp",EDGE,"E62"),sQuery(id+"F10.wireOp",EDGE,"E63"),sQuery(id+"F10.wireOp",EDGE,"E64"),sQuery(id+"F10.wireOp",EDGE,"E65"),sQuery(id+"F10.wireOp",EDGE,"E66"),sQuery(id+"F10.wireOp",EDGE,"E67"),sQuery(id+"F10.wireOp",EDGE,"E68"),sQuery(id+"F10.wireOp",EDGE,"E69"),sQuery(id+"F10.wireOp",EDGE,"E70"),sQuery(id+"F10.wireOp",EDGE,"E71"),sQuery(id+"F10.wireOp",EDGE,"E72"),sQuery(id+"F10.wireOp",EDGE,"E73"),sQuery(id+"F10.wireOp",EDGE,"E74"),sQuery(id+"F10.wireOp",EDGE,"E75"),sQuery(id+"F10.wireOp",EDGE,"E76"),sQuery(id+"F10.wireOp",EDGE,"E77"),sQuery(id+"F10.wireOp",EDGE,"E78"),sQuery(id+"F10.wireOp",EDGE,"E79"),sQuery(id+"F10.wireOp",EDGE,"E80"),sQuery(id+"F10.wireOp",EDGE,"E81"),sQuery(id+"F10.wireOp",EDGE,"E82"),sQuery(id+"F10.wireOp",EDGE,"E83"),sQuery(id+"F10.wireOp",EDGE,"E84"),sQuery(id+"F10.wireOp",EDGE,"E85"),sQuery(id+"F10.wireOp",EDGE,"E86"),sQuery(id+"F10.wireOp",EDGE,"E87"),sQuery(id+"F10.wireOp",EDGE,"E88"),sQuery(id+"F10.wireOp",EDGE,"E89"),sQuery(id+"F10.wireOp",EDGE,"E90"),sQuery(id+"F10.wireOp",EDGE,"E91"),sQuery(id+"F10.wireOp",EDGE,"E92"),sQuery(id+"F10.wireOp",EDGE,"E93"),sQuery(id+"F10.wireOp",EDGE,"E94"),sQuery(id+"F10.wireOp",EDGE,"E95"),sQuery(id+"F10.wireOp",EDGE,"E96"),sQuery(id+"F10.wireOp",EDGE,"E97"),sQuery(id+"F10.wireOp",EDGE,"E98")])]}),"instanceName":"20"});
            var Q4;
            Q4=makeQuery(id+"F18.opPattern","COPY",BODY,{"derivedFrom":makeQuery(id+"F11.opExtrude","SWEPT_BODY",BODY,{"disambiguationData":[OSD([sQuery(id+"F10.wireOp",EDGE,"E57"),sQuery(id+"F10.wireOp",EDGE,"E58"),sQuery(id+"F10.wireOp",EDGE,"E59"),sQuery(id+"F10.wireOp",EDGE,"E60"),sQuery(id+"F10.wireOp",EDGE,"E61"),sQuery(id+"F10.wireOp",EDGE,"E62"),sQuery(id+"F10.wireOp",EDGE,"E63"),sQuery(id+"F10.wireOp",EDGE,"E64"),sQuery(id+"F10.wireOp",EDGE,"E65"),sQuery(id+"F10.wireOp",EDGE,"E66"),sQuery(id+"F10.wireOp",EDGE,"E67"),sQuery(id+"F10.wireOp",EDGE,"E68"),sQuery(id+"F10.wireOp",EDGE,"E69"),sQuery(id+"F10.wireOp",EDGE,"E70"),sQuery(id+"F10.wireOp",EDGE,"E71"),sQuery(id+"F10.wireOp",EDGE,"E72"),sQuery(id+"F10.wireOp",EDGE,"E73"),sQuery(id+"F10.wireOp",EDGE,"E74"),sQuery(id+"F10.wireOp",EDGE,"E75"),sQuery(id+"F10.wireOp",EDGE,"E76"),sQuery(id+"F10.wireOp",EDGE,"E77"),sQuery(id+"F10.wireOp",EDGE,"E78"),sQuery(id+"F10.wireOp",EDGE,"E79"),sQuery(id+"F10.wireOp",EDGE,"E80"),sQuery(id+"F10.wireOp",EDGE,"E81"),sQuery(id+"F10.wireOp",EDGE,"E82"),sQuery(id+"F10.wireOp",EDGE,"E83"),sQuery(id+"F10.wireOp",EDGE,"E84"),sQuery(id+"F10.wireOp",EDGE,"E85"),sQuery(id+"F10.wireOp",EDGE,"E86"),sQuery(id+"F10.wireOp",EDGE,"E87"),sQuery(id+"F10.wireOp",EDGE,"E88"),sQuery(id+"F10.wireOp",EDGE,"E89"),sQuery(id+"F10.wireOp",EDGE,"E90"),sQuery(id+"F10.wireOp",EDGE,"E91"),sQuery(id+"F10.wireOp",EDGE,"E92"),sQuery(id+"F10.wireOp",EDGE,"E93"),sQuery(id+"F10.wireOp",EDGE,"E94"),sQuery(id+"F10.wireOp",EDGE,"E95"),sQuery(id+"F10.wireOp",EDGE,"E96"),sQuery(id+"F10.wireOp",EDGE,"E97"),sQuery(id+"F10.wireOp",EDGE,"E98")])]}),"instanceName":"19"});
            var Q5;
            Q5=makeQuery(id+"F18.opPattern","COPY",BODY,{"derivedFrom":makeQuery(id+"F11.opExtrude","SWEPT_BODY",BODY,{"disambiguationData":[OSD([sQuery(id+"F10.wireOp",EDGE,"E57"),sQuery(id+"F10.wireOp",EDGE,"E58"),sQuery(id+"F10.wireOp",EDGE,"E59"),sQuery(id+"F10.wireOp",EDGE,"E60"),sQuery(id+"F10.wireOp",EDGE,"E61"),sQuery(id+"F10.wireOp",EDGE,"E62"),sQuery(id+"F10.wireOp",EDGE,"E63"),sQuery(id+"F10.wireOp",EDGE,"E64"),sQuery(id+"F10.wireOp",EDGE,"E65"),sQuery(id+"F10.wireOp",EDGE,"E66"),sQuery(id+"F10.wireOp",EDGE,"E67"),sQuery(id+"F10.wireOp",EDGE,"E68"),sQuery(id+"F10.wireOp",EDGE,"E69"),sQuery(id+"F10.wireOp",EDGE,"E70"),sQuery(id+"F10.wireOp",EDGE,"E71"),sQuery(id+"F10.wireOp",EDGE,"E72"),sQuery(id+"F10.wireOp",EDGE,"E73"),sQuery(id+"F10.wireOp",EDGE,"E74"),sQuery(id+"F10.wireOp",EDGE,"E75"),sQuery(id+"F10.wireOp",EDGE,"E76"),sQuery(id+"F10.wireOp",EDGE,"E77"),sQuery(id+"F10.wireOp",EDGE,"E78"),sQuery(id+"F10.wireOp",EDGE,"E79"),sQuery(id+"F10.wireOp",EDGE,"E80"),sQuery(id+"F10.wireOp",EDGE,"E81"),sQuery(id+"F10.wireOp",EDGE,"E82"),sQuery(id+"F10.wireOp",EDGE,"E83"),sQuery(id+"F10.wireOp",EDGE,"E84"),sQuery(id+"F10.wireOp",EDGE,"E85"),sQuery(id+"F10.wireOp",EDGE,"E86"),sQuery(id+"F10.wireOp",EDGE,"E87"),sQuery(id+"F10.wireOp",EDGE,"E88"),sQuery(id+"F10.wireOp",EDGE,"E89"),sQuery(id+"F10.wireOp",EDGE,"E90"),sQuery(id+"F10.wireOp",EDGE,"E91"),sQuery(id+"F10.wireOp",EDGE,"E92"),sQuery(id+"F10.wireOp",EDGE,"E93"),sQuery(id+"F10.wireOp",EDGE,"E94"),sQuery(id+"F10.wireOp",EDGE,"E95"),sQuery(id+"F10.wireOp",EDGE,"E96"),sQuery(id+"F10.wireOp",EDGE,"E97"),sQuery(id+"F10.wireOp",EDGE,"E98")])]}),"instanceName":"18"});
            var Q6;
            Q6=makeQuery(id+"F18.opPattern","COPY",BODY,{"derivedFrom":makeQuery(id+"F11.opExtrude","SWEPT_BODY",BODY,{"disambiguationData":[OSD([sQuery(id+"F10.wireOp",EDGE,"E57"),sQuery(id+"F10.wireOp",EDGE,"E58"),sQuery(id+"F10.wireOp",EDGE,"E59"),sQuery(id+"F10.wireOp",EDGE,"E60"),sQuery(id+"F10.wireOp",EDGE,"E61"),sQuery(id+"F10.wireOp",EDGE,"E62"),sQuery(id+"F10.wireOp",EDGE,"E63"),sQuery(id+"F10.wireOp",EDGE,"E64"),sQuery(id+"F10.wireOp",EDGE,"E65"),sQuery(id+"F10.wireOp",EDGE,"E66"),sQuery(id+"F10.wireOp",EDGE,"E67"),sQuery(id+"F10.wireOp",EDGE,"E68"),sQuery(id+"F10.wireOp",EDGE,"E69"),sQuery(id+"F10.wireOp",EDGE,"E70"),sQuery(id+"F10.wireOp",EDGE,"E71"),sQuery(id+"F10.wireOp",EDGE,"E72"),sQuery(id+"F10.wireOp",EDGE,"E73"),sQuery(id+"F10.wireOp",EDGE,"E74"),sQuery(id+"F10.wireOp",EDGE,"E75"),sQuery(id+"F10.wireOp",EDGE,"E76"),sQuery(id+"F10.wireOp",EDGE,"E77"),sQuery(id+"F10.wireOp",EDGE,"E78"),sQuery(id+"F10.wireOp",EDGE,"E79"),sQuery(id+"F10.wireOp",EDGE,"E80"),sQuery(id+"F10.wireOp",EDGE,"E81"),sQuery(id+"F10.wireOp",EDGE,"E82"),sQuery(id+"F10.wireOp",EDGE,"E83"),sQuery(id+"F10.wireOp",EDGE,"E84"),sQuery(id+"F10.wireOp",EDGE,"E85"),sQuery(id+"F10.wireOp",EDGE,"E86"),sQuery(id+"F10.wireOp",EDGE,"E87"),sQuery(id+"F10.wireOp",EDGE,"E88"),sQuery(id+"F10.wireOp",EDGE,"E89"),sQuery(id+"F10.wireOp",EDGE,"E90"),sQuery(id+"F10.wireOp",EDGE,"E91"),sQuery(id+"F10.wireOp",EDGE,"E92"),sQuery(id+"F10.wireOp",EDGE,"E93"),sQuery(id+"F10.wireOp",EDGE,"E94"),sQuery(id+"F10.wireOp",EDGE,"E95"),sQuery(id+"F10.wireOp",EDGE,"E96"),sQuery(id+"F10.wireOp",EDGE,"E97"),sQuery(id+"F10.wireOp",EDGE,"E98")])]}),"instanceName":"17"});
            var Q7;
            Q7=makeQuery(id+"F18.opPattern","COPY",BODY,{"derivedFrom":makeQuery(id+"F11.opExtrude","SWEPT_BODY",BODY,{"disambiguationData":[OSD([sQuery(id+"F10.wireOp",EDGE,"E57"),sQuery(id+"F10.wireOp",EDGE,"E58"),sQuery(id+"F10.wireOp",EDGE,"E59"),sQuery(id+"F10.wireOp",EDGE,"E60"),sQuery(id+"F10.wireOp",EDGE,"E61"),sQuery(id+"F10.wireOp",EDGE,"E62"),sQuery(id+"F10.wireOp",EDGE,"E63"),sQuery(id+"F10.wireOp",EDGE,"E64"),sQuery(id+"F10.wireOp",EDGE,"E65"),sQuery(id+"F10.wireOp",EDGE,"E66"),sQuery(id+"F10.wireOp",EDGE,"E67"),sQuery(id+"F10.wireOp",EDGE,"E68"),sQuery(id+"F10.wireOp",EDGE,"E69"),sQuery(id+"F10.wireOp",EDGE,"E70"),sQuery(id+"F10.wireOp",EDGE,"E71"),sQuery(id+"F10.wireOp",EDGE,"E72"),sQuery(id+"F10.wireOp",EDGE,"E73"),sQuery(id+"F10.wireOp",EDGE,"E74"),sQuery(id+"F10.wireOp",EDGE,"E75"),sQuery(id+"F10.wireOp",EDGE,"E76"),sQuery(id+"F10.wireOp",EDGE,"E77"),sQuery(id+"F10.wireOp",EDGE,"E78"),sQuery(id+"F10.wireOp",EDGE,"E79"),sQuery(id+"F10.wireOp",EDGE,"E80"),sQuery(id+"F10.wireOp",EDGE,"E81"),sQuery(id+"F10.wireOp",EDGE,"E82"),sQuery(id+"F10.wireOp",EDGE,"E83"),sQuery(id+"F10.wireOp",EDGE,"E84"),sQuery(id+"F10.wireOp",EDGE,"E85"),sQuery(id+"F10.wireOp",EDGE,"E86"),sQuery(id+"F10.wireOp",EDGE,"E87"),sQuery(id+"F10.wireOp",EDGE,"E88"),sQuery(id+"F10.wireOp",EDGE,"E89"),sQuery(id+"F10.wireOp",EDGE,"E90"),sQuery(id+"F10.wireOp",EDGE,"E91"),sQuery(id+"F10.wireOp",EDGE,"E92"),sQuery(id+"F10.wireOp",EDGE,"E93"),sQuery(id+"F10.wireOp",EDGE,"E94"),sQuery(id+"F10.wireOp",EDGE,"E95"),sQuery(id+"F10.wireOp",EDGE,"E96"),sQuery(id+"F10.wireOp",EDGE,"E97"),sQuery(id+"F10.wireOp",EDGE,"E98")])]}),"instanceName":"16"});
            var Q8;
            Q8=makeQuery(id+"F18.opPattern","COPY",BODY,{"derivedFrom":makeQuery(id+"F11.opExtrude","SWEPT_BODY",BODY,{"disambiguationData":[OSD([sQuery(id+"F10.wireOp",EDGE,"E57"),sQuery(id+"F10.wireOp",EDGE,"E58"),sQuery(id+"F10.wireOp",EDGE,"E59"),sQuery(id+"F10.wireOp",EDGE,"E60"),sQuery(id+"F10.wireOp",EDGE,"E61"),sQuery(id+"F10.wireOp",EDGE,"E62"),sQuery(id+"F10.wireOp",EDGE,"E63"),sQuery(id+"F10.wireOp",EDGE,"E64"),sQuery(id+"F10.wireOp",EDGE,"E65"),sQuery(id+"F10.wireOp",EDGE,"E66"),sQuery(id+"F10.wireOp",EDGE,"E67"),sQuery(id+"F10.wireOp",EDGE,"E68"),sQuery(id+"F10.wireOp",EDGE,"E69"),sQuery(id+"F10.wireOp",EDGE,"E70"),sQuery(id+"F10.wireOp",EDGE,"E71"),sQuery(id+"F10.wireOp",EDGE,"E72"),sQuery(id+"F10.wireOp",EDGE,"E73"),sQuery(id+"F10.wireOp",EDGE,"E74"),sQuery(id+"F10.wireOp",EDGE,"E75"),sQuery(id+"F10.wireOp",EDGE,"E76"),sQuery(id+"F10.wireOp",EDGE,"E77"),sQuery(id+"F10.wireOp",EDGE,"E78"),sQuery(id+"F10.wireOp",EDGE,"E79"),sQuery(id+"F10.wireOp",EDGE,"E80"),sQuery(id+"F10.wireOp",EDGE,"E81"),sQuery(id+"F10.wireOp",EDGE,"E82"),sQuery(id+"F10.wireOp",EDGE,"E83"),sQuery(id+"F10.wireOp",EDGE,"E84"),sQuery(id+"F10.wireOp",EDGE,"E85"),sQuery(id+"F10.wireOp",EDGE,"E86"),sQuery(id+"F10.wireOp",EDGE,"E87"),sQuery(id+"F10.wireOp",EDGE,"E88"),sQuery(id+"F10.wireOp",EDGE,"E89"),sQuery(id+"F10.wireOp",EDGE,"E90"),sQuery(id+"F10.wireOp",EDGE,"E91"),sQuery(id+"F10.wireOp",EDGE,"E92"),sQuery(id+"F10.wireOp",EDGE,"E93"),sQuery(id+"F10.wireOp",EDGE,"E94"),sQuery(id+"F10.wireOp",EDGE,"E95"),sQuery(id+"F10.wireOp",EDGE,"E96"),sQuery(id+"F10.wireOp",EDGE,"E97"),sQuery(id+"F10.wireOp",EDGE,"E98")])]}),"instanceName":"15"});
            var Q9;
            Q9=makeQuery(id+"F18.opPattern","COPY",BODY,{"derivedFrom":makeQuery(id+"F11.opExtrude","SWEPT_BODY",BODY,{"disambiguationData":[OSD([sQuery(id+"F10.wireOp",EDGE,"E57"),sQuery(id+"F10.wireOp",EDGE,"E58"),sQuery(id+"F10.wireOp",EDGE,"E59"),sQuery(id+"F10.wireOp",EDGE,"E60"),sQuery(id+"F10.wireOp",EDGE,"E61"),sQuery(id+"F10.wireOp",EDGE,"E62"),sQuery(id+"F10.wireOp",EDGE,"E63"),sQuery(id+"F10.wireOp",EDGE,"E64"),sQuery(id+"F10.wireOp",EDGE,"E65"),sQuery(id+"F10.wireOp",EDGE,"E66"),sQuery(id+"F10.wireOp",EDGE,"E67"),sQuery(id+"F10.wireOp",EDGE,"E68"),sQuery(id+"F10.wireOp",EDGE,"E69"),sQuery(id+"F10.wireOp",EDGE,"E70"),sQuery(id+"F10.wireOp",EDGE,"E71"),sQuery(id+"F10.wireOp",EDGE,"E72"),sQuery(id+"F10.wireOp",EDGE,"E73"),sQuery(id+"F10.wireOp",EDGE,"E74"),sQuery(id+"F10.wireOp",EDGE,"E75"),sQuery(id+"F10.wireOp",EDGE,"E76"),sQuery(id+"F10.wireOp",EDGE,"E77"),sQuery(id+"F10.wireOp",EDGE,"E78"),sQuery(id+"F10.wireOp",EDGE,"E79"),sQuery(id+"F10.wireOp",EDGE,"E80"),sQuery(id+"F10.wireOp",EDGE,"E81"),sQuery(id+"F10.wireOp",EDGE,"E82"),sQuery(id+"F10.wireOp",EDGE,"E83"),sQuery(id+"F10.wireOp",EDGE,"E84"),sQuery(id+"F10.wireOp",EDGE,"E85"),sQuery(id+"F10.wireOp",EDGE,"E86"),sQuery(id+"F10.wireOp",EDGE,"E87"),sQuery(id+"F10.wireOp",EDGE,"E88"),sQuery(id+"F10.wireOp",EDGE,"E89"),sQuery(id+"F10.wireOp",EDGE,"E90"),sQuery(id+"F10.wireOp",EDGE,"E91"),sQuery(id+"F10.wireOp",EDGE,"E92"),sQuery(id+"F10.wireOp",EDGE,"E93"),sQuery(id+"F10.wireOp",EDGE,"E94"),sQuery(id+"F10.wireOp",EDGE,"E95"),sQuery(id+"F10.wireOp",EDGE,"E96"),sQuery(id+"F10.wireOp",EDGE,"E97"),sQuery(id+"F10.wireOp",EDGE,"E98")])]}),"instanceName":"14"});
            var Q10;
            Q10=makeQuery(id+"F1.opRevolve","SWEPT_BODY",BODY,{"disambiguationData":[OSD([sQuery(id+"F0.wireOp",EDGE,"E1"),sQuery(id+"F0.wireOp",EDGE,"E2"),sQuery(id+"F0.wireOp",EDGE,"E3"),sQuery(id+"F0.wireOp",EDGE,"E4"),sQuery(id+"F0.wireOp",EDGE,"E5"),sQuery(id+"F0.wireOp",EDGE,"E6"),sQuery(id+"F0.wireOp",EDGE,"E8"),sQuery(id+"F0.wireOp",EDGE,"E9")])]});
            booleanBodies(context, id + "F20", {"operationType" : BooleanOperationType.SUBTRACTION, "tools" : qUnion([Q0, Q1, Q2, Q3, Q4, Q5, Q6, Q7, Q8, Q9]), "targets" : qUnion([Q10])});
        }
        {
            var Q0;
            Q0=makeQuery(id+"F18.opPattern","COPY",BODY,{"derivedFrom":makeQuery(id+"F11.opExtrude","SWEPT_BODY",BODY,{"disambiguationData":[OSD([sQuery(id+"F10.wireOp",EDGE,"E57"),sQuery(id+"F10.wireOp",EDGE,"E58"),sQuery(id+"F10.wireOp",EDGE,"E59"),sQuery(id+"F10.wireOp",EDGE,"E60"),sQuery(id+"F10.wireOp",EDGE,"E61"),sQuery(id+"F10.wireOp",EDGE,"E62"),sQuery(id+"F10.wireOp",EDGE,"E63"),sQuery(id+"F10.wireOp",EDGE,"E64"),sQuery(id+"F10.wireOp",EDGE,"E65"),sQuery(id+"F10.wireOp",EDGE,"E66"),sQuery(id+"F10.wireOp",EDGE,"E67"),sQuery(id+"F10.wireOp",EDGE,"E68"),sQuery(id+"F10.wireOp",EDGE,"E69"),sQuery(id+"F10.wireOp",EDGE,"E70"),sQuery(id+"F10.wireOp",EDGE,"E71"),sQuery(id+"F10.wireOp",EDGE,"E72"),sQuery(id+"F10.wireOp",EDGE,"E73"),sQuery(id+"F10.wireOp",EDGE,"E74"),sQuery(id+"F10.wireOp",EDGE,"E75"),sQuery(id+"F10.wireOp",EDGE,"E76"),sQuery(id+"F10.wireOp",EDGE,"E77"),sQuery(id+"F10.wireOp",EDGE,"E78"),sQuery(id+"F10.wireOp",EDGE,"E79"),sQuery(id+"F10.wireOp",EDGE,"E80"),sQuery(id+"F10.wireOp",EDGE,"E81"),sQuery(id+"F10.wireOp",EDGE,"E82"),sQuery(id+"F10.wireOp",EDGE,"E83"),sQuery(id+"F10.wireOp",EDGE,"E84"),sQuery(id+"F10.wireOp",EDGE,"E85"),sQuery(id+"F10.wireOp",EDGE,"E86"),sQuery(id+"F10.wireOp",EDGE,"E87"),sQuery(id+"F10.wireOp",EDGE,"E88"),sQuery(id+"F10.wireOp",EDGE,"E89"),sQuery(id+"F10.wireOp",EDGE,"E90"),sQuery(id+"F10.wireOp",EDGE,"E91"),sQuery(id+"F10.wireOp",EDGE,"E92"),sQuery(id+"F10.wireOp",EDGE,"E93"),sQuery(id+"F10.wireOp",EDGE,"E94"),sQuery(id+"F10.wireOp",EDGE,"E95"),sQuery(id+"F10.wireOp",EDGE,"E96"),sQuery(id+"F10.wireOp",EDGE,"E97"),sQuery(id+"F10.wireOp",EDGE,"E98")])]}),"instanceName":"33"});
            var Q1;
            Q1=makeQuery(id+"F18.opPattern","COPY",BODY,{"derivedFrom":makeQuery(id+"F11.opExtrude","SWEPT_BODY",BODY,{"disambiguationData":[OSD([sQuery(id+"F10.wireOp",EDGE,"E57"),sQuery(id+"F10.wireOp",EDGE,"E58"),sQuery(id+"F10.wireOp",EDGE,"E59"),sQuery(id+"F10.wireOp",EDGE,"E60"),sQuery(id+"F10.wireOp",EDGE,"E61"),sQuery(id+"F10.wireOp",EDGE,"E62"),sQuery(id+"F10.wireOp",EDGE,"E63"),sQuery(id+"F10.wireOp",EDGE,"E64"),sQuery(id+"F10.wireOp",EDGE,"E65"),sQuery(id+"F10.wireOp",EDGE,"E66"),sQuery(id+"F10.wireOp",EDGE,"E67"),sQuery(id+"F10.wireOp",EDGE,"E68"),sQuery(id+"F10.wireOp",EDGE,"E69"),sQuery(id+"F10.wireOp",EDGE,"E70"),sQuery(id+"F10.wireOp",EDGE,"E71"),sQuery(id+"F10.wireOp",EDGE,"E72"),sQuery(id+"F10.wireOp",EDGE,"E73"),sQuery(id+"F10.wireOp",EDGE,"E74"),sQuery(id+"F10.wireOp",EDGE,"E75"),sQuery(id+"F10.wireOp",EDGE,"E76"),sQuery(id+"F10.wireOp",EDGE,"E77"),sQuery(id+"F10.wireOp",EDGE,"E78"),sQuery(id+"F10.wireOp",EDGE,"E79"),sQuery(id+"F10.wireOp",EDGE,"E80"),sQuery(id+"F10.wireOp",EDGE,"E81"),sQuery(id+"F10.wireOp",EDGE,"E82"),sQuery(id+"F10.wireOp",EDGE,"E83"),sQuery(id+"F10.wireOp",EDGE,"E84"),sQuery(id+"F10.wireOp",EDGE,"E85"),sQuery(id+"F10.wireOp",EDGE,"E86"),sQuery(id+"F10.wireOp",EDGE,"E87"),sQuery(id+"F10.wireOp",EDGE,"E88"),sQuery(id+"F10.wireOp",EDGE,"E89"),sQuery(id+"F10.wireOp",EDGE,"E90"),sQuery(id+"F10.wireOp",EDGE,"E91"),sQuery(id+"F10.wireOp",EDGE,"E92"),sQuery(id+"F10.wireOp",EDGE,"E93"),sQuery(id+"F10.wireOp",EDGE,"E94"),sQuery(id+"F10.wireOp",EDGE,"E95"),sQuery(id+"F10.wireOp",EDGE,"E96"),sQuery(id+"F10.wireOp",EDGE,"E97"),sQuery(id+"F10.wireOp",EDGE,"E98")])]}),"instanceName":"34"});
            var Q2;
            Q2=makeQuery(id+"F18.opPattern","COPY",BODY,{"derivedFrom":makeQuery(id+"F11.opExtrude","SWEPT_BODY",BODY,{"disambiguationData":[OSD([sQuery(id+"F10.wireOp",EDGE,"E57"),sQuery(id+"F10.wireOp",EDGE,"E58"),sQuery(id+"F10.wireOp",EDGE,"E59"),sQuery(id+"F10.wireOp",EDGE,"E60"),sQuery(id+"F10.wireOp",EDGE,"E61"),sQuery(id+"F10.wireOp",EDGE,"E62"),sQuery(id+"F10.wireOp",EDGE,"E63"),sQuery(id+"F10.wireOp",EDGE,"E64"),sQuery(id+"F10.wireOp",EDGE,"E65"),sQuery(id+"F10.wireOp",EDGE,"E66"),sQuery(id+"F10.wireOp",EDGE,"E67"),sQuery(id+"F10.wireOp",EDGE,"E68"),sQuery(id+"F10.wireOp",EDGE,"E69"),sQuery(id+"F10.wireOp",EDGE,"E70"),sQuery(id+"F10.wireOp",EDGE,"E71"),sQuery(id+"F10.wireOp",EDGE,"E72"),sQuery(id+"F10.wireOp",EDGE,"E73"),sQuery(id+"F10.wireOp",EDGE,"E74"),sQuery(id+"F10.wireOp",EDGE,"E75"),sQuery(id+"F10.wireOp",EDGE,"E76"),sQuery(id+"F10.wireOp",EDGE,"E77"),sQuery(id+"F10.wireOp",EDGE,"E78"),sQuery(id+"F10.wireOp",EDGE,"E79"),sQuery(id+"F10.wireOp",EDGE,"E80"),sQuery(id+"F10.wireOp",EDGE,"E81"),sQuery(id+"F10.wireOp",EDGE,"E82"),sQuery(id+"F10.wireOp",EDGE,"E83"),sQuery(id+"F10.wireOp",EDGE,"E84"),sQuery(id+"F10.wireOp",EDGE,"E85"),sQuery(id+"F10.wireOp",EDGE,"E86"),sQuery(id+"F10.wireOp",EDGE,"E87"),sQuery(id+"F10.wireOp",EDGE,"E88"),sQuery(id+"F10.wireOp",EDGE,"E89"),sQuery(id+"F10.wireOp",EDGE,"E90"),sQuery(id+"F10.wireOp",EDGE,"E91"),sQuery(id+"F10.wireOp",EDGE,"E92"),sQuery(id+"F10.wireOp",EDGE,"E93"),sQuery(id+"F10.wireOp",EDGE,"E94"),sQuery(id+"F10.wireOp",EDGE,"E95"),sQuery(id+"F10.wireOp",EDGE,"E96"),sQuery(id+"F10.wireOp",EDGE,"E97"),sQuery(id+"F10.wireOp",EDGE,"E98")])]}),"instanceName":"35"});
            var Q3;
            Q3=makeQuery(id+"F18.opPattern","COPY",BODY,{"derivedFrom":makeQuery(id+"F11.opExtrude","SWEPT_BODY",BODY,{"disambiguationData":[OSD([sQuery(id+"F10.wireOp",EDGE,"E57"),sQuery(id+"F10.wireOp",EDGE,"E58"),sQuery(id+"F10.wireOp",EDGE,"E59"),sQuery(id+"F10.wireOp",EDGE,"E60"),sQuery(id+"F10.wireOp",EDGE,"E61"),sQuery(id+"F10.wireOp",EDGE,"E62"),sQuery(id+"F10.wireOp",EDGE,"E63"),sQuery(id+"F10.wireOp",EDGE,"E64"),sQuery(id+"F10.wireOp",EDGE,"E65"),sQuery(id+"F10.wireOp",EDGE,"E66"),sQuery(id+"F10.wireOp",EDGE,"E67"),sQuery(id+"F10.wireOp",EDGE,"E68"),sQuery(id+"F10.wireOp",EDGE,"E69"),sQuery(id+"F10.wireOp",EDGE,"E70"),sQuery(id+"F10.wireOp",EDGE,"E71"),sQuery(id+"F10.wireOp",EDGE,"E72"),sQuery(id+"F10.wireOp",EDGE,"E73"),sQuery(id+"F10.wireOp",EDGE,"E74"),sQuery(id+"F10.wireOp",EDGE,"E75"),sQuery(id+"F10.wireOp",EDGE,"E76"),sQuery(id+"F10.wireOp",EDGE,"E77"),sQuery(id+"F10.wireOp",EDGE,"E78"),sQuery(id+"F10.wireOp",EDGE,"E79"),sQuery(id+"F10.wireOp",EDGE,"E80"),sQuery(id+"F10.wireOp",EDGE,"E81"),sQuery(id+"F10.wireOp",EDGE,"E82"),sQuery(id+"F10.wireOp",EDGE,"E83"),sQuery(id+"F10.wireOp",EDGE,"E84"),sQuery(id+"F10.wireOp",EDGE,"E85"),sQuery(id+"F10.wireOp",EDGE,"E86"),sQuery(id+"F10.wireOp",EDGE,"E87"),sQuery(id+"F10.wireOp",EDGE,"E88"),sQuery(id+"F10.wireOp",EDGE,"E89"),sQuery(id+"F10.wireOp",EDGE,"E90"),sQuery(id+"F10.wireOp",EDGE,"E91"),sQuery(id+"F10.wireOp",EDGE,"E92"),sQuery(id+"F10.wireOp",EDGE,"E93"),sQuery(id+"F10.wireOp",EDGE,"E94"),sQuery(id+"F10.wireOp",EDGE,"E95"),sQuery(id+"F10.wireOp",EDGE,"E96"),sQuery(id+"F10.wireOp",EDGE,"E97"),sQuery(id+"F10.wireOp",EDGE,"E98")])]}),"instanceName":"36"});
            var Q4;
            Q4=makeQuery(id+"F18.opPattern","COPY",BODY,{"derivedFrom":makeQuery(id+"F11.opExtrude","SWEPT_BODY",BODY,{"disambiguationData":[OSD([sQuery(id+"F10.wireOp",EDGE,"E57"),sQuery(id+"F10.wireOp",EDGE,"E58"),sQuery(id+"F10.wireOp",EDGE,"E59"),sQuery(id+"F10.wireOp",EDGE,"E60"),sQuery(id+"F10.wireOp",EDGE,"E61"),sQuery(id+"F10.wireOp",EDGE,"E62"),sQuery(id+"F10.wireOp",EDGE,"E63"),sQuery(id+"F10.wireOp",EDGE,"E64"),sQuery(id+"F10.wireOp",EDGE,"E65"),sQuery(id+"F10.wireOp",EDGE,"E66"),sQuery(id+"F10.wireOp",EDGE,"E67"),sQuery(id+"F10.wireOp",EDGE,"E68"),sQuery(id+"F10.wireOp",EDGE,"E69"),sQuery(id+"F10.wireOp",EDGE,"E70"),sQuery(id+"F10.wireOp",EDGE,"E71"),sQuery(id+"F10.wireOp",EDGE,"E72"),sQuery(id+"F10.wireOp",EDGE,"E73"),sQuery(id+"F10.wireOp",EDGE,"E74"),sQuery(id+"F10.wireOp",EDGE,"E75"),sQuery(id+"F10.wireOp",EDGE,"E76"),sQuery(id+"F10.wireOp",EDGE,"E77"),sQuery(id+"F10.wireOp",EDGE,"E78"),sQuery(id+"F10.wireOp",EDGE,"E79"),sQuery(id+"F10.wireOp",EDGE,"E80"),sQuery(id+"F10.wireOp",EDGE,"E81"),sQuery(id+"F10.wireOp",EDGE,"E82"),sQuery(id+"F10.wireOp",EDGE,"E83"),sQuery(id+"F10.wireOp",EDGE,"E84"),sQuery(id+"F10.wireOp",EDGE,"E85"),sQuery(id+"F10.wireOp",EDGE,"E86"),sQuery(id+"F10.wireOp",EDGE,"E87"),sQuery(id+"F10.wireOp",EDGE,"E88"),sQuery(id+"F10.wireOp",EDGE,"E89"),sQuery(id+"F10.wireOp",EDGE,"E90"),sQuery(id+"F10.wireOp",EDGE,"E91"),sQuery(id+"F10.wireOp",EDGE,"E92"),sQuery(id+"F10.wireOp",EDGE,"E93"),sQuery(id+"F10.wireOp",EDGE,"E94"),sQuery(id+"F10.wireOp",EDGE,"E95"),sQuery(id+"F10.wireOp",EDGE,"E96"),sQuery(id+"F10.wireOp",EDGE,"E97"),sQuery(id+"F10.wireOp",EDGE,"E98")])]}),"instanceName":"37"});
            var Q5;
            Q5=makeQuery(id+"F18.opPattern","COPY",BODY,{"derivedFrom":makeQuery(id+"F11.opExtrude","SWEPT_BODY",BODY,{"disambiguationData":[OSD([sQuery(id+"F10.wireOp",EDGE,"E57"),sQuery(id+"F10.wireOp",EDGE,"E58"),sQuery(id+"F10.wireOp",EDGE,"E59"),sQuery(id+"F10.wireOp",EDGE,"E60"),sQuery(id+"F10.wireOp",EDGE,"E61"),sQuery(id+"F10.wireOp",EDGE,"E62"),sQuery(id+"F10.wireOp",EDGE,"E63"),sQuery(id+"F10.wireOp",EDGE,"E64"),sQuery(id+"F10.wireOp",EDGE,"E65"),sQuery(id+"F10.wireOp",EDGE,"E66"),sQuery(id+"F10.wireOp",EDGE,"E67"),sQuery(id+"F10.wireOp",EDGE,"E68"),sQuery(id+"F10.wireOp",EDGE,"E69"),sQuery(id+"F10.wireOp",EDGE,"E70"),sQuery(id+"F10.wireOp",EDGE,"E71"),sQuery(id+"F10.wireOp",EDGE,"E72"),sQuery(id+"F10.wireOp",EDGE,"E73"),sQuery(id+"F10.wireOp",EDGE,"E74"),sQuery(id+"F10.wireOp",EDGE,"E75"),sQuery(id+"F10.wireOp",EDGE,"E76"),sQuery(id+"F10.wireOp",EDGE,"E77"),sQuery(id+"F10.wireOp",EDGE,"E78"),sQuery(id+"F10.wireOp",EDGE,"E79"),sQuery(id+"F10.wireOp",EDGE,"E80"),sQuery(id+"F10.wireOp",EDGE,"E81"),sQuery(id+"F10.wireOp",EDGE,"E82"),sQuery(id+"F10.wireOp",EDGE,"E83"),sQuery(id+"F10.wireOp",EDGE,"E84"),sQuery(id+"F10.wireOp",EDGE,"E85"),sQuery(id+"F10.wireOp",EDGE,"E86"),sQuery(id+"F10.wireOp",EDGE,"E87"),sQuery(id+"F10.wireOp",EDGE,"E88"),sQuery(id+"F10.wireOp",EDGE,"E89"),sQuery(id+"F10.wireOp",EDGE,"E90"),sQuery(id+"F10.wireOp",EDGE,"E91"),sQuery(id+"F10.wireOp",EDGE,"E92"),sQuery(id+"F10.wireOp",EDGE,"E93"),sQuery(id+"F10.wireOp",EDGE,"E94"),sQuery(id+"F10.wireOp",EDGE,"E95"),sQuery(id+"F10.wireOp",EDGE,"E96"),sQuery(id+"F10.wireOp",EDGE,"E97"),sQuery(id+"F10.wireOp",EDGE,"E98")])]}),"instanceName":"38"});
            var Q6;
            Q6=makeQuery(id+"F18.opPattern","COPY",BODY,{"derivedFrom":makeQuery(id+"F11.opExtrude","SWEPT_BODY",BODY,{"disambiguationData":[OSD([sQuery(id+"F10.wireOp",EDGE,"E57"),sQuery(id+"F10.wireOp",EDGE,"E58"),sQuery(id+"F10.wireOp",EDGE,"E59"),sQuery(id+"F10.wireOp",EDGE,"E60"),sQuery(id+"F10.wireOp",EDGE,"E61"),sQuery(id+"F10.wireOp",EDGE,"E62"),sQuery(id+"F10.wireOp",EDGE,"E63"),sQuery(id+"F10.wireOp",EDGE,"E64"),sQuery(id+"F10.wireOp",EDGE,"E65"),sQuery(id+"F10.wireOp",EDGE,"E66"),sQuery(id+"F10.wireOp",EDGE,"E67"),sQuery(id+"F10.wireOp",EDGE,"E68"),sQuery(id+"F10.wireOp",EDGE,"E69"),sQuery(id+"F10.wireOp",EDGE,"E70"),sQuery(id+"F10.wireOp",EDGE,"E71"),sQuery(id+"F10.wireOp",EDGE,"E72"),sQuery(id+"F10.wireOp",EDGE,"E73"),sQuery(id+"F10.wireOp",EDGE,"E74"),sQuery(id+"F10.wireOp",EDGE,"E75"),sQuery(id+"F10.wireOp",EDGE,"E76"),sQuery(id+"F10.wireOp",EDGE,"E77"),sQuery(id+"F10.wireOp",EDGE,"E78"),sQuery(id+"F10.wireOp",EDGE,"E79"),sQuery(id+"F10.wireOp",EDGE,"E80"),sQuery(id+"F10.wireOp",EDGE,"E81"),sQuery(id+"F10.wireOp",EDGE,"E82"),sQuery(id+"F10.wireOp",EDGE,"E83"),sQuery(id+"F10.wireOp",EDGE,"E84"),sQuery(id+"F10.wireOp",EDGE,"E85"),sQuery(id+"F10.wireOp",EDGE,"E86"),sQuery(id+"F10.wireOp",EDGE,"E87"),sQuery(id+"F10.wireOp",EDGE,"E88"),sQuery(id+"F10.wireOp",EDGE,"E89"),sQuery(id+"F10.wireOp",EDGE,"E90"),sQuery(id+"F10.wireOp",EDGE,"E91"),sQuery(id+"F10.wireOp",EDGE,"E92"),sQuery(id+"F10.wireOp",EDGE,"E93"),sQuery(id+"F10.wireOp",EDGE,"E94"),sQuery(id+"F10.wireOp",EDGE,"E95"),sQuery(id+"F10.wireOp",EDGE,"E96"),sQuery(id+"F10.wireOp",EDGE,"E97"),sQuery(id+"F10.wireOp",EDGE,"E98")])]}),"instanceName":"39"});
            var Q7;
            Q7=makeQuery(id+"F1.opRevolve","SWEPT_BODY",BODY,{"disambiguationData":[OSD([sQuery(id+"F0.wireOp",EDGE,"E1"),sQuery(id+"F0.wireOp",EDGE,"E2"),sQuery(id+"F0.wireOp",EDGE,"E3"),sQuery(id+"F0.wireOp",EDGE,"E4"),sQuery(id+"F0.wireOp",EDGE,"E5"),sQuery(id+"F0.wireOp",EDGE,"E6"),sQuery(id+"F0.wireOp",EDGE,"E8"),sQuery(id+"F0.wireOp",EDGE,"E9")])]});
            booleanBodies(context, id + "F21", {"operationType" : BooleanOperationType.SUBTRACTION, "tools" : qUnion([Q0, Q1, Q2, Q3, Q4, Q5, Q6]), "targets" : qUnion([Q7])});
        }
        {
            var Q0;
            Q0=makeQuery(id+"F11.opExtrude","SWEPT_BODY",BODY,{"disambiguationData":[OSD([sQuery(id+"F10.wireOp",EDGE,"E57"),sQuery(id+"F10.wireOp",EDGE,"E58"),sQuery(id+"F10.wireOp",EDGE,"E59"),sQuery(id+"F10.wireOp",EDGE,"E60"),sQuery(id+"F10.wireOp",EDGE,"E61"),sQuery(id+"F10.wireOp",EDGE,"E62"),sQuery(id+"F10.wireOp",EDGE,"E63"),sQuery(id+"F10.wireOp",EDGE,"E64"),sQuery(id+"F10.wireOp",EDGE,"E65"),sQuery(id+"F10.wireOp",EDGE,"E66"),sQuery(id+"F10.wireOp",EDGE,"E67"),sQuery(id+"F10.wireOp",EDGE,"E68"),sQuery(id+"F10.wireOp",EDGE,"E69"),sQuery(id+"F10.wireOp",EDGE,"E70"),sQuery(id+"F10.wireOp",EDGE,"E71"),sQuery(id+"F10.wireOp",EDGE,"E72"),sQuery(id+"F10.wireOp",EDGE,"E73"),sQuery(id+"F10.wireOp",EDGE,"E74"),sQuery(id+"F10.wireOp",EDGE,"E75"),sQuery(id+"F10.wireOp",EDGE,"E76"),sQuery(id+"F10.wireOp",EDGE,"E77"),sQuery(id+"F10.wireOp",EDGE,"E78"),sQuery(id+"F10.wireOp",EDGE,"E79"),sQuery(id+"F10.wireOp",EDGE,"E80"),sQuery(id+"F10.wireOp",EDGE,"E81"),sQuery(id+"F10.wireOp",EDGE,"E82"),sQuery(id+"F10.wireOp",EDGE,"E83"),sQuery(id+"F10.wireOp",EDGE,"E84"),sQuery(id+"F10.wireOp",EDGE,"E85"),sQuery(id+"F10.wireOp",EDGE,"E86"),sQuery(id+"F10.wireOp",EDGE,"E87"),sQuery(id+"F10.wireOp",EDGE,"E88"),sQuery(id+"F10.wireOp",EDGE,"E89"),sQuery(id+"F10.wireOp",EDGE,"E90"),sQuery(id+"F10.wireOp",EDGE,"E91"),sQuery(id+"F10.wireOp",EDGE,"E92"),sQuery(id+"F10.wireOp",EDGE,"E93"),sQuery(id+"F10.wireOp",EDGE,"E94"),sQuery(id+"F10.wireOp",EDGE,"E95"),sQuery(id+"F10.wireOp",EDGE,"E96"),sQuery(id+"F10.wireOp",EDGE,"E97"),sQuery(id+"F10.wireOp",EDGE,"E98")])]});
            var Q1;
            Q1=makeQuery(id+"F18.opPattern","COPY",BODY,{"derivedFrom":makeQuery(id+"F11.opExtrude","SWEPT_BODY",BODY,{"disambiguationData":[OSD([sQuery(id+"F10.wireOp",EDGE,"E57"),sQuery(id+"F10.wireOp",EDGE,"E58"),sQuery(id+"F10.wireOp",EDGE,"E59"),sQuery(id+"F10.wireOp",EDGE,"E60"),sQuery(id+"F10.wireOp",EDGE,"E61"),sQuery(id+"F10.wireOp",EDGE,"E62"),sQuery(id+"F10.wireOp",EDGE,"E63"),sQuery(id+"F10.wireOp",EDGE,"E64"),sQuery(id+"F10.wireOp",EDGE,"E65"),sQuery(id+"F10.wireOp",EDGE,"E66"),sQuery(id+"F10.wireOp",EDGE,"E67"),sQuery(id+"F10.wireOp",EDGE,"E68"),sQuery(id+"F10.wireOp",EDGE,"E69"),sQuery(id+"F10.wireOp",EDGE,"E70"),sQuery(id+"F10.wireOp",EDGE,"E71"),sQuery(id+"F10.wireOp",EDGE,"E72"),sQuery(id+"F10.wireOp",EDGE,"E73"),sQuery(id+"F10.wireOp",EDGE,"E74"),sQuery(id+"F10.wireOp",EDGE,"E75"),sQuery(id+"F10.wireOp",EDGE,"E76"),sQuery(id+"F10.wireOp",EDGE,"E77"),sQuery(id+"F10.wireOp",EDGE,"E78"),sQuery(id+"F10.wireOp",EDGE,"E79"),sQuery(id+"F10.wireOp",EDGE,"E80"),sQuery(id+"F10.wireOp",EDGE,"E81"),sQuery(id+"F10.wireOp",EDGE,"E82"),sQuery(id+"F10.wireOp",EDGE,"E83"),sQuery(id+"F10.wireOp",EDGE,"E84"),sQuery(id+"F10.wireOp",EDGE,"E85"),sQuery(id+"F10.wireOp",EDGE,"E86"),sQuery(id+"F10.wireOp",EDGE,"E87"),sQuery(id+"F10.wireOp",EDGE,"E88"),sQuery(id+"F10.wireOp",EDGE,"E89"),sQuery(id+"F10.wireOp",EDGE,"E90"),sQuery(id+"F10.wireOp",EDGE,"E91"),sQuery(id+"F10.wireOp",EDGE,"E92"),sQuery(id+"F10.wireOp",EDGE,"E93"),sQuery(id+"F10.wireOp",EDGE,"E94"),sQuery(id+"F10.wireOp",EDGE,"E95"),sQuery(id+"F10.wireOp",EDGE,"E96"),sQuery(id+"F10.wireOp",EDGE,"E97"),sQuery(id+"F10.wireOp",EDGE,"E98")])]}),"instanceName":"1"});
            var Q2;
            Q2=makeQuery(id+"F18.opPattern","COPY",BODY,{"derivedFrom":makeQuery(id+"F11.opExtrude","SWEPT_BODY",BODY,{"disambiguationData":[OSD([sQuery(id+"F10.wireOp",EDGE,"E57"),sQuery(id+"F10.wireOp",EDGE,"E58"),sQuery(id+"F10.wireOp",EDGE,"E59"),sQuery(id+"F10.wireOp",EDGE,"E60"),sQuery(id+"F10.wireOp",EDGE,"E61"),sQuery(id+"F10.wireOp",EDGE,"E62"),sQuery(id+"F10.wireOp",EDGE,"E63"),sQuery(id+"F10.wireOp",EDGE,"E64"),sQuery(id+"F10.wireOp",EDGE,"E65"),sQuery(id+"F10.wireOp",EDGE,"E66"),sQuery(id+"F10.wireOp",EDGE,"E67"),sQuery(id+"F10.wireOp",EDGE,"E68"),sQuery(id+"F10.wireOp",EDGE,"E69"),sQuery(id+"F10.wireOp",EDGE,"E70"),sQuery(id+"F10.wireOp",EDGE,"E71"),sQuery(id+"F10.wireOp",EDGE,"E72"),sQuery(id+"F10.wireOp",EDGE,"E73"),sQuery(id+"F10.wireOp",EDGE,"E74"),sQuery(id+"F10.wireOp",EDGE,"E75"),sQuery(id+"F10.wireOp",EDGE,"E76"),sQuery(id+"F10.wireOp",EDGE,"E77"),sQuery(id+"F10.wireOp",EDGE,"E78"),sQuery(id+"F10.wireOp",EDGE,"E79"),sQuery(id+"F10.wireOp",EDGE,"E80"),sQuery(id+"F10.wireOp",EDGE,"E81"),sQuery(id+"F10.wireOp",EDGE,"E82"),sQuery(id+"F10.wireOp",EDGE,"E83"),sQuery(id+"F10.wireOp",EDGE,"E84"),sQuery(id+"F10.wireOp",EDGE,"E85"),sQuery(id+"F10.wireOp",EDGE,"E86"),sQuery(id+"F10.wireOp",EDGE,"E87"),sQuery(id+"F10.wireOp",EDGE,"E88"),sQuery(id+"F10.wireOp",EDGE,"E89"),sQuery(id+"F10.wireOp",EDGE,"E90"),sQuery(id+"F10.wireOp",EDGE,"E91"),sQuery(id+"F10.wireOp",EDGE,"E92"),sQuery(id+"F10.wireOp",EDGE,"E93"),sQuery(id+"F10.wireOp",EDGE,"E94"),sQuery(id+"F10.wireOp",EDGE,"E95"),sQuery(id+"F10.wireOp",EDGE,"E96"),sQuery(id+"F10.wireOp",EDGE,"E97"),sQuery(id+"F10.wireOp",EDGE,"E98")])]}),"instanceName":"2"});
            var Q3;
            Q3=makeQuery(id+"F18.opPattern","COPY",BODY,{"derivedFrom":makeQuery(id+"F11.opExtrude","SWEPT_BODY",BODY,{"disambiguationData":[OSD([sQuery(id+"F10.wireOp",EDGE,"E57"),sQuery(id+"F10.wireOp",EDGE,"E58"),sQuery(id+"F10.wireOp",EDGE,"E59"),sQuery(id+"F10.wireOp",EDGE,"E60"),sQuery(id+"F10.wireOp",EDGE,"E61"),sQuery(id+"F10.wireOp",EDGE,"E62"),sQuery(id+"F10.wireOp",EDGE,"E63"),sQuery(id+"F10.wireOp",EDGE,"E64"),sQuery(id+"F10.wireOp",EDGE,"E65"),sQuery(id+"F10.wireOp",EDGE,"E66"),sQuery(id+"F10.wireOp",EDGE,"E67"),sQuery(id+"F10.wireOp",EDGE,"E68"),sQuery(id+"F10.wireOp",EDGE,"E69"),sQuery(id+"F10.wireOp",EDGE,"E70"),sQuery(id+"F10.wireOp",EDGE,"E71"),sQuery(id+"F10.wireOp",EDGE,"E72"),sQuery(id+"F10.wireOp",EDGE,"E73"),sQuery(id+"F10.wireOp",EDGE,"E74"),sQuery(id+"F10.wireOp",EDGE,"E75"),sQuery(id+"F10.wireOp",EDGE,"E76"),sQuery(id+"F10.wireOp",EDGE,"E77"),sQuery(id+"F10.wireOp",EDGE,"E78"),sQuery(id+"F10.wireOp",EDGE,"E79"),sQuery(id+"F10.wireOp",EDGE,"E80"),sQuery(id+"F10.wireOp",EDGE,"E81"),sQuery(id+"F10.wireOp",EDGE,"E82"),sQuery(id+"F10.wireOp",EDGE,"E83"),sQuery(id+"F10.wireOp",EDGE,"E84"),sQuery(id+"F10.wireOp",EDGE,"E85"),sQuery(id+"F10.wireOp",EDGE,"E86"),sQuery(id+"F10.wireOp",EDGE,"E87"),sQuery(id+"F10.wireOp",EDGE,"E88"),sQuery(id+"F10.wireOp",EDGE,"E89"),sQuery(id+"F10.wireOp",EDGE,"E90"),sQuery(id+"F10.wireOp",EDGE,"E91"),sQuery(id+"F10.wireOp",EDGE,"E92"),sQuery(id+"F10.wireOp",EDGE,"E93"),sQuery(id+"F10.wireOp",EDGE,"E94"),sQuery(id+"F10.wireOp",EDGE,"E95"),sQuery(id+"F10.wireOp",EDGE,"E96"),sQuery(id+"F10.wireOp",EDGE,"E97"),sQuery(id+"F10.wireOp",EDGE,"E98")])]}),"instanceName":"3"});
            var Q4;
            Q4=makeQuery(id+"F18.opPattern","COPY",BODY,{"derivedFrom":makeQuery(id+"F11.opExtrude","SWEPT_BODY",BODY,{"disambiguationData":[OSD([sQuery(id+"F10.wireOp",EDGE,"E57"),sQuery(id+"F10.wireOp",EDGE,"E58"),sQuery(id+"F10.wireOp",EDGE,"E59"),sQuery(id+"F10.wireOp",EDGE,"E60"),sQuery(id+"F10.wireOp",EDGE,"E61"),sQuery(id+"F10.wireOp",EDGE,"E62"),sQuery(id+"F10.wireOp",EDGE,"E63"),sQuery(id+"F10.wireOp",EDGE,"E64"),sQuery(id+"F10.wireOp",EDGE,"E65"),sQuery(id+"F10.wireOp",EDGE,"E66"),sQuery(id+"F10.wireOp",EDGE,"E67"),sQuery(id+"F10.wireOp",EDGE,"E68"),sQuery(id+"F10.wireOp",EDGE,"E69"),sQuery(id+"F10.wireOp",EDGE,"E70"),sQuery(id+"F10.wireOp",EDGE,"E71"),sQuery(id+"F10.wireOp",EDGE,"E72"),sQuery(id+"F10.wireOp",EDGE,"E73"),sQuery(id+"F10.wireOp",EDGE,"E74"),sQuery(id+"F10.wireOp",EDGE,"E75"),sQuery(id+"F10.wireOp",EDGE,"E76"),sQuery(id+"F10.wireOp",EDGE,"E77"),sQuery(id+"F10.wireOp",EDGE,"E78"),sQuery(id+"F10.wireOp",EDGE,"E79"),sQuery(id+"F10.wireOp",EDGE,"E80"),sQuery(id+"F10.wireOp",EDGE,"E81"),sQuery(id+"F10.wireOp",EDGE,"E82"),sQuery(id+"F10.wireOp",EDGE,"E83"),sQuery(id+"F10.wireOp",EDGE,"E84"),sQuery(id+"F10.wireOp",EDGE,"E85"),sQuery(id+"F10.wireOp",EDGE,"E86"),sQuery(id+"F10.wireOp",EDGE,"E87"),sQuery(id+"F10.wireOp",EDGE,"E88"),sQuery(id+"F10.wireOp",EDGE,"E89"),sQuery(id+"F10.wireOp",EDGE,"E90"),sQuery(id+"F10.wireOp",EDGE,"E91"),sQuery(id+"F10.wireOp",EDGE,"E92"),sQuery(id+"F10.wireOp",EDGE,"E93"),sQuery(id+"F10.wireOp",EDGE,"E94"),sQuery(id+"F10.wireOp",EDGE,"E95"),sQuery(id+"F10.wireOp",EDGE,"E96"),sQuery(id+"F10.wireOp",EDGE,"E97"),sQuery(id+"F10.wireOp",EDGE,"E98")])]}),"instanceName":"4"});
            var Q5;
            Q5=makeQuery(id+"F18.opPattern","COPY",BODY,{"derivedFrom":makeQuery(id+"F11.opExtrude","SWEPT_BODY",BODY,{"disambiguationData":[OSD([sQuery(id+"F10.wireOp",EDGE,"E57"),sQuery(id+"F10.wireOp",EDGE,"E58"),sQuery(id+"F10.wireOp",EDGE,"E59"),sQuery(id+"F10.wireOp",EDGE,"E60"),sQuery(id+"F10.wireOp",EDGE,"E61"),sQuery(id+"F10.wireOp",EDGE,"E62"),sQuery(id+"F10.wireOp",EDGE,"E63"),sQuery(id+"F10.wireOp",EDGE,"E64"),sQuery(id+"F10.wireOp",EDGE,"E65"),sQuery(id+"F10.wireOp",EDGE,"E66"),sQuery(id+"F10.wireOp",EDGE,"E67"),sQuery(id+"F10.wireOp",EDGE,"E68"),sQuery(id+"F10.wireOp",EDGE,"E69"),sQuery(id+"F10.wireOp",EDGE,"E70"),sQuery(id+"F10.wireOp",EDGE,"E71"),sQuery(id+"F10.wireOp",EDGE,"E72"),sQuery(id+"F10.wireOp",EDGE,"E73"),sQuery(id+"F10.wireOp",EDGE,"E74"),sQuery(id+"F10.wireOp",EDGE,"E75"),sQuery(id+"F10.wireOp",EDGE,"E76"),sQuery(id+"F10.wireOp",EDGE,"E77"),sQuery(id+"F10.wireOp",EDGE,"E78"),sQuery(id+"F10.wireOp",EDGE,"E79"),sQuery(id+"F10.wireOp",EDGE,"E80"),sQuery(id+"F10.wireOp",EDGE,"E81"),sQuery(id+"F10.wireOp",EDGE,"E82"),sQuery(id+"F10.wireOp",EDGE,"E83"),sQuery(id+"F10.wireOp",EDGE,"E84"),sQuery(id+"F10.wireOp",EDGE,"E85"),sQuery(id+"F10.wireOp",EDGE,"E86"),sQuery(id+"F10.wireOp",EDGE,"E87"),sQuery(id+"F10.wireOp",EDGE,"E88"),sQuery(id+"F10.wireOp",EDGE,"E89"),sQuery(id+"F10.wireOp",EDGE,"E90"),sQuery(id+"F10.wireOp",EDGE,"E91"),sQuery(id+"F10.wireOp",EDGE,"E92"),sQuery(id+"F10.wireOp",EDGE,"E93"),sQuery(id+"F10.wireOp",EDGE,"E94"),sQuery(id+"F10.wireOp",EDGE,"E95"),sQuery(id+"F10.wireOp",EDGE,"E96"),sQuery(id+"F10.wireOp",EDGE,"E97"),sQuery(id+"F10.wireOp",EDGE,"E98")])]}),"instanceName":"5"});
            var Q6;
            Q6=makeQuery(id+"F18.opPattern","COPY",BODY,{"derivedFrom":makeQuery(id+"F11.opExtrude","SWEPT_BODY",BODY,{"disambiguationData":[OSD([sQuery(id+"F10.wireOp",EDGE,"E57"),sQuery(id+"F10.wireOp",EDGE,"E58"),sQuery(id+"F10.wireOp",EDGE,"E59"),sQuery(id+"F10.wireOp",EDGE,"E60"),sQuery(id+"F10.wireOp",EDGE,"E61"),sQuery(id+"F10.wireOp",EDGE,"E62"),sQuery(id+"F10.wireOp",EDGE,"E63"),sQuery(id+"F10.wireOp",EDGE,"E64"),sQuery(id+"F10.wireOp",EDGE,"E65"),sQuery(id+"F10.wireOp",EDGE,"E66"),sQuery(id+"F10.wireOp",EDGE,"E67"),sQuery(id+"F10.wireOp",EDGE,"E68"),sQuery(id+"F10.wireOp",EDGE,"E69"),sQuery(id+"F10.wireOp",EDGE,"E70"),sQuery(id+"F10.wireOp",EDGE,"E71"),sQuery(id+"F10.wireOp",EDGE,"E72"),sQuery(id+"F10.wireOp",EDGE,"E73"),sQuery(id+"F10.wireOp",EDGE,"E74"),sQuery(id+"F10.wireOp",EDGE,"E75"),sQuery(id+"F10.wireOp",EDGE,"E76"),sQuery(id+"F10.wireOp",EDGE,"E77"),sQuery(id+"F10.wireOp",EDGE,"E78"),sQuery(id+"F10.wireOp",EDGE,"E79"),sQuery(id+"F10.wireOp",EDGE,"E80"),sQuery(id+"F10.wireOp",EDGE,"E81"),sQuery(id+"F10.wireOp",EDGE,"E82"),sQuery(id+"F10.wireOp",EDGE,"E83"),sQuery(id+"F10.wireOp",EDGE,"E84"),sQuery(id+"F10.wireOp",EDGE,"E85"),sQuery(id+"F10.wireOp",EDGE,"E86"),sQuery(id+"F10.wireOp",EDGE,"E87"),sQuery(id+"F10.wireOp",EDGE,"E88"),sQuery(id+"F10.wireOp",EDGE,"E89"),sQuery(id+"F10.wireOp",EDGE,"E90"),sQuery(id+"F10.wireOp",EDGE,"E91"),sQuery(id+"F10.wireOp",EDGE,"E92"),sQuery(id+"F10.wireOp",EDGE,"E93"),sQuery(id+"F10.wireOp",EDGE,"E94"),sQuery(id+"F10.wireOp",EDGE,"E95"),sQuery(id+"F10.wireOp",EDGE,"E96"),sQuery(id+"F10.wireOp",EDGE,"E97"),sQuery(id+"F10.wireOp",EDGE,"E98")])]}),"instanceName":"6"});
            var Q7;
            Q7=makeQuery(id+"F18.opPattern","COPY",BODY,{"derivedFrom":makeQuery(id+"F11.opExtrude","SWEPT_BODY",BODY,{"disambiguationData":[OSD([sQuery(id+"F10.wireOp",EDGE,"E57"),sQuery(id+"F10.wireOp",EDGE,"E58"),sQuery(id+"F10.wireOp",EDGE,"E59"),sQuery(id+"F10.wireOp",EDGE,"E60"),sQuery(id+"F10.wireOp",EDGE,"E61"),sQuery(id+"F10.wireOp",EDGE,"E62"),sQuery(id+"F10.wireOp",EDGE,"E63"),sQuery(id+"F10.wireOp",EDGE,"E64"),sQuery(id+"F10.wireOp",EDGE,"E65"),sQuery(id+"F10.wireOp",EDGE,"E66"),sQuery(id+"F10.wireOp",EDGE,"E67"),sQuery(id+"F10.wireOp",EDGE,"E68"),sQuery(id+"F10.wireOp",EDGE,"E69"),sQuery(id+"F10.wireOp",EDGE,"E70"),sQuery(id+"F10.wireOp",EDGE,"E71"),sQuery(id+"F10.wireOp",EDGE,"E72"),sQuery(id+"F10.wireOp",EDGE,"E73"),sQuery(id+"F10.wireOp",EDGE,"E74"),sQuery(id+"F10.wireOp",EDGE,"E75"),sQuery(id+"F10.wireOp",EDGE,"E76"),sQuery(id+"F10.wireOp",EDGE,"E77"),sQuery(id+"F10.wireOp",EDGE,"E78"),sQuery(id+"F10.wireOp",EDGE,"E79"),sQuery(id+"F10.wireOp",EDGE,"E80"),sQuery(id+"F10.wireOp",EDGE,"E81"),sQuery(id+"F10.wireOp",EDGE,"E82"),sQuery(id+"F10.wireOp",EDGE,"E83"),sQuery(id+"F10.wireOp",EDGE,"E84"),sQuery(id+"F10.wireOp",EDGE,"E85"),sQuery(id+"F10.wireOp",EDGE,"E86"),sQuery(id+"F10.wireOp",EDGE,"E87"),sQuery(id+"F10.wireOp",EDGE,"E88"),sQuery(id+"F10.wireOp",EDGE,"E89"),sQuery(id+"F10.wireOp",EDGE,"E90"),sQuery(id+"F10.wireOp",EDGE,"E91"),sQuery(id+"F10.wireOp",EDGE,"E92"),sQuery(id+"F10.wireOp",EDGE,"E93"),sQuery(id+"F10.wireOp",EDGE,"E94"),sQuery(id+"F10.wireOp",EDGE,"E95"),sQuery(id+"F10.wireOp",EDGE,"E96"),sQuery(id+"F10.wireOp",EDGE,"E97"),sQuery(id+"F10.wireOp",EDGE,"E98")])]}),"instanceName":"7"});
            var Q8;
            Q8=makeQuery(id+"F18.opPattern","COPY",BODY,{"derivedFrom":makeQuery(id+"F11.opExtrude","SWEPT_BODY",BODY,{"disambiguationData":[OSD([sQuery(id+"F10.wireOp",EDGE,"E57"),sQuery(id+"F10.wireOp",EDGE,"E58"),sQuery(id+"F10.wireOp",EDGE,"E59"),sQuery(id+"F10.wireOp",EDGE,"E60"),sQuery(id+"F10.wireOp",EDGE,"E61"),sQuery(id+"F10.wireOp",EDGE,"E62"),sQuery(id+"F10.wireOp",EDGE,"E63"),sQuery(id+"F10.wireOp",EDGE,"E64"),sQuery(id+"F10.wireOp",EDGE,"E65"),sQuery(id+"F10.wireOp",EDGE,"E66"),sQuery(id+"F10.wireOp",EDGE,"E67"),sQuery(id+"F10.wireOp",EDGE,"E68"),sQuery(id+"F10.wireOp",EDGE,"E69"),sQuery(id+"F10.wireOp",EDGE,"E70"),sQuery(id+"F10.wireOp",EDGE,"E71"),sQuery(id+"F10.wireOp",EDGE,"E72"),sQuery(id+"F10.wireOp",EDGE,"E73"),sQuery(id+"F10.wireOp",EDGE,"E74"),sQuery(id+"F10.wireOp",EDGE,"E75"),sQuery(id+"F10.wireOp",EDGE,"E76"),sQuery(id+"F10.wireOp",EDGE,"E77"),sQuery(id+"F10.wireOp",EDGE,"E78"),sQuery(id+"F10.wireOp",EDGE,"E79"),sQuery(id+"F10.wireOp",EDGE,"E80"),sQuery(id+"F10.wireOp",EDGE,"E81"),sQuery(id+"F10.wireOp",EDGE,"E82"),sQuery(id+"F10.wireOp",EDGE,"E83"),sQuery(id+"F10.wireOp",EDGE,"E84"),sQuery(id+"F10.wireOp",EDGE,"E85"),sQuery(id+"F10.wireOp",EDGE,"E86"),sQuery(id+"F10.wireOp",EDGE,"E87"),sQuery(id+"F10.wireOp",EDGE,"E88"),sQuery(id+"F10.wireOp",EDGE,"E89"),sQuery(id+"F10.wireOp",EDGE,"E90"),sQuery(id+"F10.wireOp",EDGE,"E91"),sQuery(id+"F10.wireOp",EDGE,"E92"),sQuery(id+"F10.wireOp",EDGE,"E93"),sQuery(id+"F10.wireOp",EDGE,"E94"),sQuery(id+"F10.wireOp",EDGE,"E95"),sQuery(id+"F10.wireOp",EDGE,"E96"),sQuery(id+"F10.wireOp",EDGE,"E97"),sQuery(id+"F10.wireOp",EDGE,"E98")])]}),"instanceName":"8"});
            var Q9;
            Q9=makeQuery(id+"F18.opPattern","COPY",BODY,{"derivedFrom":makeQuery(id+"F11.opExtrude","SWEPT_BODY",BODY,{"disambiguationData":[OSD([sQuery(id+"F10.wireOp",EDGE,"E57"),sQuery(id+"F10.wireOp",EDGE,"E58"),sQuery(id+"F10.wireOp",EDGE,"E59"),sQuery(id+"F10.wireOp",EDGE,"E60"),sQuery(id+"F10.wireOp",EDGE,"E61"),sQuery(id+"F10.wireOp",EDGE,"E62"),sQuery(id+"F10.wireOp",EDGE,"E63"),sQuery(id+"F10.wireOp",EDGE,"E64"),sQuery(id+"F10.wireOp",EDGE,"E65"),sQuery(id+"F10.wireOp",EDGE,"E66"),sQuery(id+"F10.wireOp",EDGE,"E67"),sQuery(id+"F10.wireOp",EDGE,"E68"),sQuery(id+"F10.wireOp",EDGE,"E69"),sQuery(id+"F10.wireOp",EDGE,"E70"),sQuery(id+"F10.wireOp",EDGE,"E71"),sQuery(id+"F10.wireOp",EDGE,"E72"),sQuery(id+"F10.wireOp",EDGE,"E73"),sQuery(id+"F10.wireOp",EDGE,"E74"),sQuery(id+"F10.wireOp",EDGE,"E75"),sQuery(id+"F10.wireOp",EDGE,"E76"),sQuery(id+"F10.wireOp",EDGE,"E77"),sQuery(id+"F10.wireOp",EDGE,"E78"),sQuery(id+"F10.wireOp",EDGE,"E79"),sQuery(id+"F10.wireOp",EDGE,"E80"),sQuery(id+"F10.wireOp",EDGE,"E81"),sQuery(id+"F10.wireOp",EDGE,"E82"),sQuery(id+"F10.wireOp",EDGE,"E83"),sQuery(id+"F10.wireOp",EDGE,"E84"),sQuery(id+"F10.wireOp",EDGE,"E85"),sQuery(id+"F10.wireOp",EDGE,"E86"),sQuery(id+"F10.wireOp",EDGE,"E87"),sQuery(id+"F10.wireOp",EDGE,"E88"),sQuery(id+"F10.wireOp",EDGE,"E89"),sQuery(id+"F10.wireOp",EDGE,"E90"),sQuery(id+"F10.wireOp",EDGE,"E91"),sQuery(id+"F10.wireOp",EDGE,"E92"),sQuery(id+"F10.wireOp",EDGE,"E93"),sQuery(id+"F10.wireOp",EDGE,"E94"),sQuery(id+"F10.wireOp",EDGE,"E95"),sQuery(id+"F10.wireOp",EDGE,"E96"),sQuery(id+"F10.wireOp",EDGE,"E97"),sQuery(id+"F10.wireOp",EDGE,"E98")])]}),"instanceName":"9"});
            var Q10;
            Q10=makeQuery(id+"F18.opPattern","COPY",BODY,{"derivedFrom":makeQuery(id+"F11.opExtrude","SWEPT_BODY",BODY,{"disambiguationData":[OSD([sQuery(id+"F10.wireOp",EDGE,"E57"),sQuery(id+"F10.wireOp",EDGE,"E58"),sQuery(id+"F10.wireOp",EDGE,"E59"),sQuery(id+"F10.wireOp",EDGE,"E60"),sQuery(id+"F10.wireOp",EDGE,"E61"),sQuery(id+"F10.wireOp",EDGE,"E62"),sQuery(id+"F10.wireOp",EDGE,"E63"),sQuery(id+"F10.wireOp",EDGE,"E64"),sQuery(id+"F10.wireOp",EDGE,"E65"),sQuery(id+"F10.wireOp",EDGE,"E66"),sQuery(id+"F10.wireOp",EDGE,"E67"),sQuery(id+"F10.wireOp",EDGE,"E68"),sQuery(id+"F10.wireOp",EDGE,"E69"),sQuery(id+"F10.wireOp",EDGE,"E70"),sQuery(id+"F10.wireOp",EDGE,"E71"),sQuery(id+"F10.wireOp",EDGE,"E72"),sQuery(id+"F10.wireOp",EDGE,"E73"),sQuery(id+"F10.wireOp",EDGE,"E74"),sQuery(id+"F10.wireOp",EDGE,"E75"),sQuery(id+"F10.wireOp",EDGE,"E76"),sQuery(id+"F10.wireOp",EDGE,"E77"),sQuery(id+"F10.wireOp",EDGE,"E78"),sQuery(id+"F10.wireOp",EDGE,"E79"),sQuery(id+"F10.wireOp",EDGE,"E80"),sQuery(id+"F10.wireOp",EDGE,"E81"),sQuery(id+"F10.wireOp",EDGE,"E82"),sQuery(id+"F10.wireOp",EDGE,"E83"),sQuery(id+"F10.wireOp",EDGE,"E84"),sQuery(id+"F10.wireOp",EDGE,"E85"),sQuery(id+"F10.wireOp",EDGE,"E86"),sQuery(id+"F10.wireOp",EDGE,"E87"),sQuery(id+"F10.wireOp",EDGE,"E88"),sQuery(id+"F10.wireOp",EDGE,"E89"),sQuery(id+"F10.wireOp",EDGE,"E90"),sQuery(id+"F10.wireOp",EDGE,"E91"),sQuery(id+"F10.wireOp",EDGE,"E92"),sQuery(id+"F10.wireOp",EDGE,"E93"),sQuery(id+"F10.wireOp",EDGE,"E94"),sQuery(id+"F10.wireOp",EDGE,"E95"),sQuery(id+"F10.wireOp",EDGE,"E96"),sQuery(id+"F10.wireOp",EDGE,"E97"),sQuery(id+"F10.wireOp",EDGE,"E98")])]}),"instanceName":"10"});
            var Q11;
            Q11=makeQuery(id+"F18.opPattern","COPY",BODY,{"derivedFrom":makeQuery(id+"F11.opExtrude","SWEPT_BODY",BODY,{"disambiguationData":[OSD([sQuery(id+"F10.wireOp",EDGE,"E57"),sQuery(id+"F10.wireOp",EDGE,"E58"),sQuery(id+"F10.wireOp",EDGE,"E59"),sQuery(id+"F10.wireOp",EDGE,"E60"),sQuery(id+"F10.wireOp",EDGE,"E61"),sQuery(id+"F10.wireOp",EDGE,"E62"),sQuery(id+"F10.wireOp",EDGE,"E63"),sQuery(id+"F10.wireOp",EDGE,"E64"),sQuery(id+"F10.wireOp",EDGE,"E65"),sQuery(id+"F10.wireOp",EDGE,"E66"),sQuery(id+"F10.wireOp",EDGE,"E67"),sQuery(id+"F10.wireOp",EDGE,"E68"),sQuery(id+"F10.wireOp",EDGE,"E69"),sQuery(id+"F10.wireOp",EDGE,"E70"),sQuery(id+"F10.wireOp",EDGE,"E71"),sQuery(id+"F10.wireOp",EDGE,"E72"),sQuery(id+"F10.wireOp",EDGE,"E73"),sQuery(id+"F10.wireOp",EDGE,"E74"),sQuery(id+"F10.wireOp",EDGE,"E75"),sQuery(id+"F10.wireOp",EDGE,"E76"),sQuery(id+"F10.wireOp",EDGE,"E77"),sQuery(id+"F10.wireOp",EDGE,"E78"),sQuery(id+"F10.wireOp",EDGE,"E79"),sQuery(id+"F10.wireOp",EDGE,"E80"),sQuery(id+"F10.wireOp",EDGE,"E81"),sQuery(id+"F10.wireOp",EDGE,"E82"),sQuery(id+"F10.wireOp",EDGE,"E83"),sQuery(id+"F10.wireOp",EDGE,"E84"),sQuery(id+"F10.wireOp",EDGE,"E85"),sQuery(id+"F10.wireOp",EDGE,"E86"),sQuery(id+"F10.wireOp",EDGE,"E87"),sQuery(id+"F10.wireOp",EDGE,"E88"),sQuery(id+"F10.wireOp",EDGE,"E89"),sQuery(id+"F10.wireOp",EDGE,"E90"),sQuery(id+"F10.wireOp",EDGE,"E91"),sQuery(id+"F10.wireOp",EDGE,"E92"),sQuery(id+"F10.wireOp",EDGE,"E93"),sQuery(id+"F10.wireOp",EDGE,"E94"),sQuery(id+"F10.wireOp",EDGE,"E95"),sQuery(id+"F10.wireOp",EDGE,"E96"),sQuery(id+"F10.wireOp",EDGE,"E97"),sQuery(id+"F10.wireOp",EDGE,"E98")])]}),"instanceName":"11"});
            var Q12;
            Q12=makeQuery(id+"F18.opPattern","COPY",BODY,{"derivedFrom":makeQuery(id+"F11.opExtrude","SWEPT_BODY",BODY,{"disambiguationData":[OSD([sQuery(id+"F10.wireOp",EDGE,"E57"),sQuery(id+"F10.wireOp",EDGE,"E58"),sQuery(id+"F10.wireOp",EDGE,"E59"),sQuery(id+"F10.wireOp",EDGE,"E60"),sQuery(id+"F10.wireOp",EDGE,"E61"),sQuery(id+"F10.wireOp",EDGE,"E62"),sQuery(id+"F10.wireOp",EDGE,"E63"),sQuery(id+"F10.wireOp",EDGE,"E64"),sQuery(id+"F10.wireOp",EDGE,"E65"),sQuery(id+"F10.wireOp",EDGE,"E66"),sQuery(id+"F10.wireOp",EDGE,"E67"),sQuery(id+"F10.wireOp",EDGE,"E68"),sQuery(id+"F10.wireOp",EDGE,"E69"),sQuery(id+"F10.wireOp",EDGE,"E70"),sQuery(id+"F10.wireOp",EDGE,"E71"),sQuery(id+"F10.wireOp",EDGE,"E72"),sQuery(id+"F10.wireOp",EDGE,"E73"),sQuery(id+"F10.wireOp",EDGE,"E74"),sQuery(id+"F10.wireOp",EDGE,"E75"),sQuery(id+"F10.wireOp",EDGE,"E76"),sQuery(id+"F10.wireOp",EDGE,"E77"),sQuery(id+"F10.wireOp",EDGE,"E78"),sQuery(id+"F10.wireOp",EDGE,"E79"),sQuery(id+"F10.wireOp",EDGE,"E80"),sQuery(id+"F10.wireOp",EDGE,"E81"),sQuery(id+"F10.wireOp",EDGE,"E82"),sQuery(id+"F10.wireOp",EDGE,"E83"),sQuery(id+"F10.wireOp",EDGE,"E84"),sQuery(id+"F10.wireOp",EDGE,"E85"),sQuery(id+"F10.wireOp",EDGE,"E86"),sQuery(id+"F10.wireOp",EDGE,"E87"),sQuery(id+"F10.wireOp",EDGE,"E88"),sQuery(id+"F10.wireOp",EDGE,"E89"),sQuery(id+"F10.wireOp",EDGE,"E90"),sQuery(id+"F10.wireOp",EDGE,"E91"),sQuery(id+"F10.wireOp",EDGE,"E92"),sQuery(id+"F10.wireOp",EDGE,"E93"),sQuery(id+"F10.wireOp",EDGE,"E94"),sQuery(id+"F10.wireOp",EDGE,"E95"),sQuery(id+"F10.wireOp",EDGE,"E96"),sQuery(id+"F10.wireOp",EDGE,"E97"),sQuery(id+"F10.wireOp",EDGE,"E98")])]}),"instanceName":"12"});
            var Q13;
            Q13=makeQuery(id+"F18.opPattern","COPY",BODY,{"derivedFrom":makeQuery(id+"F11.opExtrude","SWEPT_BODY",BODY,{"disambiguationData":[OSD([sQuery(id+"F10.wireOp",EDGE,"E57"),sQuery(id+"F10.wireOp",EDGE,"E58"),sQuery(id+"F10.wireOp",EDGE,"E59"),sQuery(id+"F10.wireOp",EDGE,"E60"),sQuery(id+"F10.wireOp",EDGE,"E61"),sQuery(id+"F10.wireOp",EDGE,"E62"),sQuery(id+"F10.wireOp",EDGE,"E63"),sQuery(id+"F10.wireOp",EDGE,"E64"),sQuery(id+"F10.wireOp",EDGE,"E65"),sQuery(id+"F10.wireOp",EDGE,"E66"),sQuery(id+"F10.wireOp",EDGE,"E67"),sQuery(id+"F10.wireOp",EDGE,"E68"),sQuery(id+"F10.wireOp",EDGE,"E69"),sQuery(id+"F10.wireOp",EDGE,"E70"),sQuery(id+"F10.wireOp",EDGE,"E71"),sQuery(id+"F10.wireOp",EDGE,"E72"),sQuery(id+"F10.wireOp",EDGE,"E73"),sQuery(id+"F10.wireOp",EDGE,"E74"),sQuery(id+"F10.wireOp",EDGE,"E75"),sQuery(id+"F10.wireOp",EDGE,"E76"),sQuery(id+"F10.wireOp",EDGE,"E77"),sQuery(id+"F10.wireOp",EDGE,"E78"),sQuery(id+"F10.wireOp",EDGE,"E79"),sQuery(id+"F10.wireOp",EDGE,"E80"),sQuery(id+"F10.wireOp",EDGE,"E81"),sQuery(id+"F10.wireOp",EDGE,"E82"),sQuery(id+"F10.wireOp",EDGE,"E83"),sQuery(id+"F10.wireOp",EDGE,"E84"),sQuery(id+"F10.wireOp",EDGE,"E85"),sQuery(id+"F10.wireOp",EDGE,"E86"),sQuery(id+"F10.wireOp",EDGE,"E87"),sQuery(id+"F10.wireOp",EDGE,"E88"),sQuery(id+"F10.wireOp",EDGE,"E89"),sQuery(id+"F10.wireOp",EDGE,"E90"),sQuery(id+"F10.wireOp",EDGE,"E91"),sQuery(id+"F10.wireOp",EDGE,"E92"),sQuery(id+"F10.wireOp",EDGE,"E93"),sQuery(id+"F10.wireOp",EDGE,"E94"),sQuery(id+"F10.wireOp",EDGE,"E95"),sQuery(id+"F10.wireOp",EDGE,"E96"),sQuery(id+"F10.wireOp",EDGE,"E97"),sQuery(id+"F10.wireOp",EDGE,"E98")])]}),"instanceName":"13"});
            var Q14;
            Q14=makeQuery(id+"F1.opRevolve","SWEPT_BODY",BODY,{"disambiguationData":[OSD([sQuery(id+"F0.wireOp",EDGE,"E1"),sQuery(id+"F0.wireOp",EDGE,"E2"),sQuery(id+"F0.wireOp",EDGE,"E3"),sQuery(id+"F0.wireOp",EDGE,"E4"),sQuery(id+"F0.wireOp",EDGE,"E5"),sQuery(id+"F0.wireOp",EDGE,"E6"),sQuery(id+"F0.wireOp",EDGE,"E8"),sQuery(id+"F0.wireOp",EDGE,"E9")])]});
            booleanBodies(context, id + "F22", {"operationType" : BooleanOperationType.SUBTRACTION, "tools" : qUnion([Q0, Q1, Q2, Q3, Q4, Q5, Q6, Q7, Q8, Q9, Q10, Q11, Q12, Q13]), "targets" : qUnion([Q14])});
        }
    });
